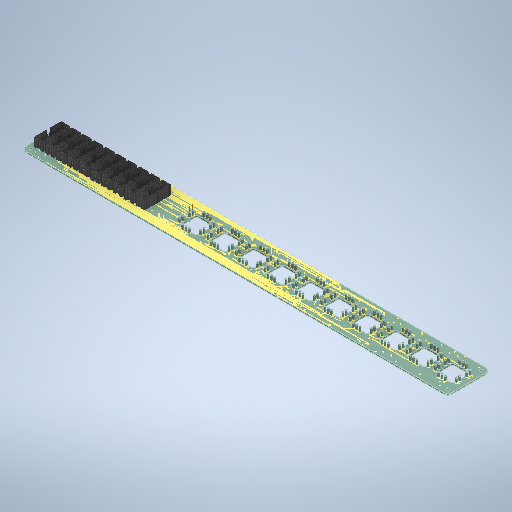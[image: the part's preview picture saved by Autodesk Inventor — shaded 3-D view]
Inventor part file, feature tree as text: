
AUTODESK INVENTOR PART (.ipt)
format: ipt  version: 2025.2 (Build 292293000, 293)  size: 19,431,936 bytes
history: native  units: mm
features: other x2, extrude x1, pattern_linear x1, sketch x1
ambient origin geometry x8: Origin, YZ Plane, XZ Plane, XY Plane, X Axis, Y Axis, Z Axis, Center Point
bodies: Volumenkörper1 (feature_tree), Volumenkörper2 (feature_tree), Volumenkörper3 (feature_tree), Volumenkörper4 (feature_tree), Volumenkörper5 (feature_tree), Volumenkörper6 (feature_tree), Volumenkörper7 (feature_tree), Volumenkörper8 (feature_tree), Volumenkörper9 (feature_tree), Volumenkörper10 (feature_tree), Volumenkörper11 (feature_tree), Volumenkörper12 (feature_tree), Volumenkörper13 (feature_tree), Volumenkörper14 (feature_tree), Volumenkörper15 (feature_tree), Volumenkörper16 (feature_tree), Volumenkörper17 (feature_tree), Volumenkörper18 (feature_tree), Volumenkörper19 (feature_tree), Volumenkörper20 (feature_tree), Volumenkörper21 (feature_tree), Volumenkörper22 (feature_tree), Volumenkörper23 (feature_tree), Volumenkörper24 (feature_tree), Volumenkörper25 (feature_tree), Volumenkörper26 (feature_tree), Volumenkörper27 (feature_tree), Volumenkörper28 (feature_tree), Volumenkörper29 (feature_tree), Volumenkörper30 (feature_tree), Volumenkörper31 (feature_tree), Volumenkörper32 (feature_tree), Volumenkörper33 (feature_tree), Volumenkörper34 (feature_tree), Volumenkörper35 (feature_tree), Volumenkörper36 (feature_tree), Volumenkörper37 (feature_tree), Volumenkörper38 (feature_tree), Volumenkörper39 (feature_tree), Volumenkörper40 (feature_tree), Volumenkörper41 (feature_tree), Volumenkörper42 (feature_tree), Volumenkörper43 (feature_tree), Volumenkörper44 (feature_tree), Volumenkörper45 (feature_tree), Volumenkörper46 (feature_tree), Volumenkörper47 (feature_tree), Volumenkörper48 (feature_tree), Volumenkörper49 (feature_tree), Volumenkörper50 (feature_tree), Volumenkörper51 (feature_tree), Volumenkörper52 (feature_tree), Volumenkörper53 (feature_tree), Volumenkörper54 (feature_tree), Volumenkörper55 (feature_tree), Volumenkörper56 (feature_tree), Volumenkörper57 (feature_tree), Volumenkörper58 (feature_tree), Volumenkörper59 (feature_tree), Volumenkörper60 (feature_tree), Volumenkörper61 (feature_tree), Volumenkörper62 (feature_tree), Volumenkörper63 (feature_tree), Volumenkörper64 (feature_tree), Volumenkörper65 (feature_tree), Volumenkörper66 (feature_tree), Volumenkörper67 (feature_tree), Volumenkörper68 (feature_tree), Volumenkörper69 (feature_tree), Volumenkörper70 (feature_tree), Volumenkörper71 (feature_tree), Volumenkörper72 (feature_tree), Volumenkörper73 (feature_tree), Volumenkörper74 (feature_tree), Volumenkörper75 (feature_tree), Volumenkörper76 (feature_tree), Volumenkörper77 (feature_tree), Volumenkörper78 (feature_tree), Volumenkörper79 (feature_tree), Volumenkörper80 (feature_tree), Volumenkörper81 (feature_tree), Volumenkörper82 (feature_tree), Volumenkörper83 (feature_tree), Volumenkörper84 (feature_tree), Volumenkörper85 (feature_tree), Volumenkörper86 (feature_tree), Volumenkörper87 (feature_tree), Volumenkörper88 (feature_tree), Volumenkörper89 (feature_tree), Volumenkörper90 (feature_tree), Volumenkörper91 (feature_tree), Volumenkörper92 (feature_tree), Volumenkörper93 (feature_tree), Volumenkörper94 (feature_tree), Volumenkörper95 (feature_tree), Volumenkörper96 (feature_tree), Volumenkörper97 (feature_tree), Volumenkörper98 (feature_tree), Volumenkörper99 (feature_tree), Volumenkörper100 (feature_tree), Volumenkörper101 (feature_tree), Volumenkörper102 (feature_tree), Volumenkörper103 (feature_tree), Volumenkörper104 (feature_tree), Volumenkörper105 (feature_tree), Volumenkörper106 (feature_tree), Volumenkörper107 (feature_tree), Volumenkörper108 (feature_tree), Volumenkörper109 (feature_tree), Volumenkörper110 (feature_tree), Volumenkörper111 (feature_tree), Volumenkörper112 (feature_tree), Volumenkörper113 (feature_tree), Volumenkörper114 (feature_tree), Volumenkörper115 (feature_tree), Volumenkörper116 (feature_tree), Volumenkörper117 (feature_tree), Volumenkörper118 (feature_tree), Volumenkörper119 (feature_tree), Volumenkörper120 (feature_tree), Volumenkörper121 (feature_tree), Volumenkörper122 (feature_tree), Volumenkörper123 (feature_tree), Volumenkörper124 (feature_tree), Volumenkörper125 (feature_tree), Volumenkörper126 (feature_tree), Volumenkörper127 (feature_tree), Volumenkörper128 (feature_tree), Volumenkörper129 (feature_tree), Volumenkörper130 (feature_tree), Volumenkörper131 (feature_tree), Volumenkörper132 (feature_tree), Volumenkörper133 (feature_tree), Volumenkörper134 (feature_tree), Volumenkörper135 (feature_tree), Volumenkörper136 (feature_tree), Volumenkörper137 (feature_tree), Volumenkörper138 (feature_tree), Volumenkörper139 (feature_tree), Volumenkörper140 (feature_tree), Volumenkörper141 (feature_tree), Volumenkörper142 (feature_tree), Volumenkörper143 (feature_tree), Volumenkörper144 (feature_tree), Volumenkörper145 (feature_tree), Volumenkörper146 (feature_tree), Volumenkörper147 (feature_tree), Volumenkörper148 (feature_tree), Volumenkörper149 (feature_tree), Volumenkörper150 (feature_tree), Volumenkörper151 (feature_tree), Volumenkörper152 (feature_tree), Volumenkörper153 (feature_tree), Volumenkörper154 (feature_tree), Volumenkörper155 (feature_tree), Volumenkörper156 (feature_tree), Volumenkörper157 (feature_tree), Volumenkörper158 (feature_tree), Volumenkörper159 (feature_tree), Volumenkörper160 (feature_tree), Volumenkörper161 (feature_tree), Volumenkörper162 (feature_tree), Volumenkörper163 (feature_tree), Volumenkörper164 (feature_tree), Volumenkörper165 (feature_tree), Volumenkörper166 (feature_tree), Volumenkörper167 (feature_tree), Volumenkörper168 (feature_tree), Volumenkörper169 (feature_tree), Volumenkörper170 (feature_tree), Volumenkörper171 (feature_tree), Volumenkörper172 (feature_tree), Volumenkörper173 (feature_tree), Volumenkörper174 (feature_tree), Volumenkörper175 (feature_tree), Volumenkörper176 (feature_tree), Volumenkörper177 (feature_tree), Volumenkörper178 (feature_tree), Volumenkörper179 (feature_tree), Volumenkörper180 (feature_tree), Volumenkörper181 (feature_tree), Volumenkörper182 (feature_tree), Volumenkörper183 (feature_tree), Volumenkörper184 (feature_tree), Volumenkörper185 (feature_tree), Volumenkörper186 (feature_tree), Volumenkörper187 (feature_tree), Volumenkörper188 (feature_tree), Volumenkörper189 (feature_tree), Volumenkörper190 (feature_tree), Volumenkörper191 (feature_tree), Volumenkörper192 (feature_tree), Volumenkörper193 (feature_tree), Volumenkörper194 (feature_tree), Volumenkörper195 (feature_tree), Volumenkörper196 (feature_tree), Volumenkörper197 (feature_tree), Volumenkörper198 (feature_tree), Volumenkörper199 (feature_tree), Volumenkörper200 (feature_tree), Volumenkörper201 (feature_tree), Volumenkörper202 (feature_tree), Volumenkörper203 (feature_tree), Volumenkörper204 (feature_tree), Volumenkörper205 (feature_tree), Volumenkörper206 (feature_tree), Volumenkörper207 (feature_tree), Volumenkörper208 (feature_tree), Volumenkörper209 (feature_tree), Volumenkörper210 (feature_tree), Volumenkörper211 (feature_tree), Volumenkörper212 (feature_tree), Volumenkörper213 (feature_tree), Volumenkörper214 (feature_tree), Volumenkörper215 (feature_tree), Volumenkörper216 (feature_tree), Volumenkörper217 (feature_tree), Volumenkörper218 (feature_tree), Volumenkörper219 (feature_tree), Volumenkörper220 (feature_tree), Volumenkörper221 (feature_tree), Volumenkörper222 (feature_tree), Volumenkörper223 (feature_tree), Volumenkörper224 (feature_tree), Volumenkörper225 (feature_tree), Volumenkörper226 (feature_tree), Volumenkörper227 (feature_tree), Volumenkörper228 (feature_tree), Volumenkörper229 (feature_tree), Volumenkörper230 (feature_tree), Volumenkörper231 (feature_tree), Volumenkörper232 (feature_tree), Volumenkörper233 (feature_tree), Volumenkörper234 (feature_tree), Volumenkörper235 (feature_tree), Volumenkörper236 (feature_tree), Volumenkörper237 (feature_tree), Volumenkörper238 (feature_tree), Volumenkörper239 (feature_tree), Volumenkörper240 (feature_tree), Volumenkörper241 (feature_tree), Volumenkörper242 (feature_tree), Volumenkörper243 (feature_tree), Volumenkörper244 (feature_tree), Volumenkörper245 (feature_tree), Volumenkörper246 (feature_tree), Volumenkörper247 (feature_tree), Volumenkörper248 (feature_tree), Volumenkörper249 (feature_tree), Volumenkörper250 (feature_tree), Volumenkörper251 (feature_tree), Volumenkörper252 (feature_tree), Volumenkörper253 (feature_tree), Volumenkörper254 (feature_tree), Volumenkörper255 (feature_tree), Volumenkörper256 (feature_tree), Volumenkörper257 (feature_tree), Volumenkörper258 (feature_tree), Volumenkörper259 (feature_tree), Volumenkörper260 (feature_tree), Volumenkörper261 (feature_tree), Volumenkörper262 (feature_tree), Volumenkörper263 (feature_tree), Volumenkörper264 (feature_tree), Volumenkörper265 (feature_tree), Volumenkörper266 (feature_tree), Volumenkörper267 (feature_tree), Volumenkörper268 (feature_tree), Volumenkörper269 (feature_tree), Volumenkörper270 (feature_tree), Volumenkörper271 (feature_tree), Volumenkörper272 (feature_tree), Volumenkörper273 (feature_tree), Volumenkörper274 (feature_tree), Volumenkörper275 (feature_tree), Volumenkörper276 (feature_tree), Volumenkörper277 (feature_tree), Volumenkörper278 (feature_tree), Volumenkörper279 (feature_tree), Volumenkörper280 (feature_tree), Volumenkörper281 (feature_tree), Volumenkörper282 (feature_tree), Volumenkörper283 (feature_tree), Volumenkörper284 (feature_tree), Volumenkörper285 (feature_tree), Volumenkörper286 (feature_tree), Volumenkörper287 (feature_tree), Volumenkörper288 (feature_tree), Volumenkörper289 (feature_tree), Volumenkörper290 (feature_tree), Volumenkörper291 (feature_tree), Volumenkörper292 (feature_tree), Volumenkörper293 (feature_tree), Volumenkörper294 (feature_tree), Volumenkörper295 (feature_tree), Volumenkörper296 (feature_tree), Volumenkörper297 (feature_tree), Volumenkörper298 (feature_tree), Volumenkörper299 (feature_tree), Volumenkörper300 (feature_tree), Volumenkörper301 (feature_tree), Volumenkörper302 (feature_tree), Volumenkörper303 (feature_tree), Volumenkörper304 (feature_tree), Volumenkörper305 (feature_tree), Volumenkörper306 (feature_tree), Volumenkörper307 (feature_tree), Volumenkörper308 (feature_tree), Volumenkörper309 (feature_tree), Volumenkörper310 (feature_tree), Volumenkörper311 (feature_tree), Volumenkörper312 (feature_tree), Volumenkörper313 (feature_tree), Volumenkörper314 (feature_tree), Volumenkörper315 (feature_tree), Volumenkörper316 (feature_tree), Volumenkörper317 (feature_tree), Volumenkörper318 (feature_tree), Volumenkörper319 (feature_tree), Volumenkörper320 (feature_tree), Volumenkörper321 (feature_tree), Volumenkörper322 (feature_tree), Volumenkörper323 (feature_tree), Volumenkörper324 (feature_tree), Volumenkörper325 (feature_tree), Volumenkörper326 (feature_tree), Volumenkörper327 (feature_tree), Volumenkörper328 (feature_tree), Volumenkörper329 (feature_tree), Volumenkörper330 (feature_tree), Volumenkörper331 (feature_tree), Volumenkörper332 (feature_tree), Volumenkörper333 (feature_tree), Volumenkörper334 (feature_tree), Volumenkörper335 (feature_tree), Volumenkörper336 (feature_tree), Volumenkörper337 (feature_tree), Volumenkörper338 (feature_tree), Volumenkörper339 (feature_tree), Volumenkörper340 (feature_tree), Volumenkörper341 (feature_tree), Volumenkörper342 (feature_tree), Volumenkörper343 (feature_tree), Volumenkörper344 (feature_tree), Volumenkörper345 (feature_tree), Volumenkörper346 (feature_tree), Volumenkörper347 (feature_tree), Volumenkörper348 (feature_tree), Volumenkörper349 (feature_tree), Volumenkörper350 (feature_tree), Volumenkörper351 (feature_tree), Volumenkörper352 (feature_tree), Volumenkörper353 (feature_tree), Volumenkörper354 (feature_tree), Volumenkörper355 (feature_tree), Volumenkörper356 (feature_tree), Volumenkörper357 (feature_tree), Volumenkörper358 (feature_tree), Volumenkörper359 (feature_tree), Volumenkörper360 (feature_tree), Volumenkörper361 (feature_tree), Volumenkörper362 (feature_tree), Volumenkörper363 (feature_tree), Volumenkörper364 (feature_tree), Volumenkörper365 (feature_tree), Volumenkörper366 (feature_tree), Volumenkörper367 (feature_tree), Volumenkörper368 (feature_tree), Volumenkörper369 (feature_tree), Volumenkörper370 (feature_tree), Volumenkörper371 (feature_tree), Volumenkörper372 (feature_tree), Volumenkörper373 (feature_tree), Volumenkörper374 (feature_tree), Volumenkörper375 (feature_tree), Volumenkörper376 (feature_tree), Volumenkörper377 (feature_tree), Volumenkörper378 (feature_tree), Volumenkörper379 (feature_tree), Volumenkörper380 (feature_tree), Volumenkörper381 (feature_tree), Volumenkörper382 (feature_tree), Volumenkörper383 (feature_tree), Volumenkörper384 (feature_tree), Volumenkörper385 (feature_tree), Volumenkörper386 (feature_tree), Volumenkörper387 (feature_tree), Volumenkörper388 (feature_tree), Volumenkörper389 (feature_tree), Volumenkörper390 (feature_tree), Volumenkörper391 (feature_tree), Volumenkörper392 (feature_tree), Volumenkörper393 (feature_tree), Volumenkörper394 (feature_tree), Volumenkörper395 (feature_tree), Volumenkörper396 (feature_tree), Volumenkörper397 (feature_tree), Volumenkörper398 (feature_tree), Volumenkörper399 (feature_tree), Volumenkörper400 (feature_tree), Volumenkörper401 (feature_tree), Volumenkörper402 (feature_tree), Volumenkörper403 (feature_tree), Volumenkörper404 (feature_tree), Volumenkörper405 (feature_tree), Volumenkörper406 (feature_tree), Volumenkörper407 (feature_tree), Volumenkörper408 (feature_tree), Volumenkörper409 (feature_tree), Volumenkörper410 (feature_tree), Volumenkörper411 (feature_tree), Volumenkörper412 (feature_tree), Volumenkörper413 (feature_tree), Volumenkörper414 (feature_tree), Volumenkörper415 (feature_tree), Volumenkörper416 (feature_tree), Volumenkörper417 (feature_tree), Volumenkörper418 (feature_tree), Volumenkörper419 (feature_tree), Volumenkörper420 (feature_tree), Volumenkörper421 (feature_tree), Volumenkörper422 (feature_tree), Volumenkörper423 (feature_tree), Volumenkörper424 (feature_tree), Volumenkörper425 (feature_tree), Volumenkörper426 (feature_tree), Volumenkörper427 (feature_tree), Volumenkörper428 (feature_tree), Volumenkörper429 (feature_tree), Volumenkörper430 (feature_tree), Volumenkörper431 (feature_tree), Volumenkörper432 (feature_tree), Volumenkörper433 (feature_tree), Volumenkörper434 (feature_tree), Volumenkörper435 (feature_tree), Volumenkörper436 (feature_tree), Volumenkörper437 (feature_tree), Volumenkörper438 (feature_tree), Volumenkörper439 (feature_tree), Volumenkörper440 (feature_tree), Volumenkörper441 (feature_tree), Volumenkörper442 (feature_tree), Volumenkörper443 (feature_tree), Volumenkörper444 (feature_tree), Volumenkörper445 (feature_tree), Volumenkörper446 (feature_tree), Volumenkörper447 (feature_tree), Volumenkörper448 (feature_tree), Volumenkörper449 (feature_tree), Volumenkörper450 (feature_tree), Volumenkörper451 (feature_tree), Volumenkörper452 (feature_tree), Volumenkörper453 (feature_tree), Volumenkörper454 (feature_tree), Volumenkörper455 (feature_tree), Volumenkörper456 (feature_tree), Volumenkörper457 (feature_tree), Volumenkörper458 (feature_tree), Volumenkörper459 (feature_tree), Volumenkörper460 (feature_tree), Volumenkörper461 (feature_tree), Volumenkörper462 (feature_tree), Volumenkörper463 (feature_tree), Volumenkörper464 (feature_tree), Volumenkörper465 (feature_tree), Volumenkörper466 (feature_tree), Volumenkörper467 (feature_tree), Volumenkörper468 (feature_tree), Volumenkörper469 (feature_tree), Volumenkörper470 (feature_tree), Volumenkörper471 (feature_tree), Volumenkörper472 (feature_tree), Volumenkörper473 (feature_tree), Volumenkörper474 (feature_tree), Volumenkörper475 (feature_tree), Volumenkörper476 (feature_tree), Volumenkörper477 (feature_tree), Volumenkörper478 (feature_tree), Volumenkörper479 (feature_tree), Volumenkörper480 (feature_tree), Volumenkörper481 (feature_tree), Volumenkörper482 (feature_tree), Volumenkörper483 (feature_tree), Volumenkörper484 (feature_tree), Volumenkörper485 (feature_tree), Volumenkörper486 (feature_tree), Volumenkörper487 (feature_tree), Volumenkörper488 (feature_tree), Volumenkörper489 (feature_tree), Volumenkörper490 (feature_tree), Volumenkörper491 (feature_tree), Volumenkörper492 (feature_tree), Volumenkörper493 (feature_tree), Volumenkörper494 (feature_tree), Volumenkörper495 (feature_tree), Volumenkörper496 (feature_tree), Volumenkörper497 (feature_tree), Volumenkörper498 (feature_tree), Volumenkörper499 (feature_tree), Volumenkörper500 (feature_tree), Volumenkörper501 (feature_tree), Volumenkörper502 (feature_tree), Volumenkörper503 (feature_tree), Volumenkörper504 (feature_tree), Volumenkörper505 (feature_tree), Volumenkörper506 (feature_tree), Volumenkörper507 (feature_tree), Volumenkörper508 (feature_tree), Volumenkörper509 (feature_tree), Volumenkörper510 (feature_tree), Volumenkörper511 (feature_tree), Volumenkörper512 (feature_tree), Volumenkörper513 (feature_tree), Volumenkörper514 (feature_tree), Volumenkörper515 (feature_tree), Volumenkörper516 (feature_tree), Volumenkörper517 (feature_tree), Volumenkörper518 (feature_tree), Volumenkörper519 (feature_tree), Volumenkörper520 (feature_tree), Volumenkörper521 (feature_tree), Volumenkörper522 (feature_tree), Volumenkörper523 (feature_tree), Volumenkörper524 (feature_tree), Volumenkörper525 (feature_tree), Volumenkörper526 (feature_tree), Volumenkörper527 (feature_tree), Volumenkörper528 (feature_tree), Volumenkörper529 (feature_tree), Volumenkörper530 (feature_tree), Volumenkörper531 (feature_tree), Volumenkörper532 (feature_tree), Volumenkörper533 (feature_tree), Volumenkörper534 (feature_tree), Volumenkörper535 (feature_tree), Volumenkörper536 (feature_tree), Volumenkörper537 (feature_tree), Volumenkörper538 (feature_tree), Volumenkörper539 (feature_tree), Volumenkörper540 (feature_tree), Volumenkörper541 (feature_tree), Volumenkörper542 (feature_tree), Volumenkörper543 (feature_tree), Volumenkörper544 (feature_tree), Volumenkörper545 (feature_tree), Volumenkörper546 (feature_tree), Volumenkörper547 (feature_tree), Volumenkörper548 (feature_tree), Volumenkörper549 (feature_tree), Volumenkörper550 (feature_tree), Volumenkörper551 (feature_tree), Volumenkörper552 (feature_tree), Volumenkörper553 (feature_tree), Volumenkörper554 (feature_tree), Volumenkörper555 (feature_tree), Volumenkörper556 (feature_tree), Volumenkörper557 (feature_tree), Volumenkörper558 (feature_tree), Volumenkörper559 (feature_tree), Volumenkörper560 (feature_tree), Volumenkörper561 (feature_tree), Volumenkörper562 (feature_tree), Volumenkörper563 (feature_tree), Volumenkörper564 (feature_tree), Volumenkörper565 (feature_tree), Volumenkörper566 (feature_tree), Volumenkörper567 (feature_tree), Volumenkörper568 (feature_tree), Volumenkörper569 (feature_tree), Volumenkörper570 (feature_tree), Volumenkörper571 (feature_tree), Volumenkörper572 (feature_tree), Volumenkörper573 (feature_tree), Volumenkörper574 (feature_tree), Volumenkörper575 (feature_tree), Volumenkörper576 (feature_tree), Volumenkörper577 (feature_tree), Volumenkörper578 (feature_tree), Volumenkörper579 (feature_tree), Volumenkörper580 (feature_tree), Volumenkörper581 (feature_tree), Volumenkörper582 (feature_tree), Volumenkörper583 (feature_tree), Volumenkörper584 (feature_tree), Volumenkörper585 (feature_tree), Volumenkörper586 (feature_tree), Volumenkörper587 (feature_tree), Volumenkörper588 (feature_tree), Volumenkörper589 (feature_tree), Volumenkörper590 (feature_tree), Volumenkörper591 (feature_tree), Volumenkörper592 (feature_tree), Volumenkörper593 (feature_tree), Volumenkörper594 (feature_tree), Volumenkörper595 (feature_tree), Volumenkörper596 (feature_tree), Volumenkörper597 (feature_tree), Volumenkörper598 (feature_tree), Volumenkörper599 (feature_tree), Volumenkörper600 (feature_tree), Volumenkörper601 (feature_tree), Volumenkörper602 (feature_tree), Volumenkörper603 (feature_tree), Volumenkörper604 (feature_tree), Volumenkörper605 (feature_tree), Volumenkörper606 (feature_tree), Volumenkörper607 (feature_tree), Volumenkörper608 (feature_tree), Volumenkörper609 (feature_tree), Volumenkörper610 (feature_tree), Volumenkörper611 (feature_tree), Volumenkörper612 (feature_tree), Volumenkörper613 (feature_tree), Volumenkörper614 (feature_tree), Volumenkörper615 (feature_tree), Volumenkörper616 (feature_tree), Volumenkörper617 (feature_tree), Volumenkörper618 (feature_tree), Volumenkörper619 (feature_tree), Volumenkörper620 (feature_tree), Volumenkörper621 (feature_tree), Volumenkörper622 (feature_tree), Volumenkörper623 (feature_tree), Volumenkörper624 (feature_tree), Volumenkörper625 (feature_tree), Volumenkörper626 (feature_tree), Volumenkörper627 (feature_tree), Volumenkörper628 (feature_tree), Volumenkörper629 (feature_tree), Volumenkörper630 (feature_tree), Volumenkörper631 (feature_tree), Volumenkörper632 (feature_tree), Volumenkörper633 (feature_tree), Volumenkörper634 (feature_tree), Volumenkörper635 (feature_tree), Volumenkörper636 (feature_tree), Volumenkörper637 (feature_tree), Volumenkörper638 (feature_tree), Volumenkörper639 (feature_tree), Volumenkörper640 (feature_tree), Volumenkörper641 (feature_tree), Volumenkörper642 (feature_tree), Volumenkörper643 (feature_tree), Volumenkörper644 (feature_tree), Volumenkörper645 (feature_tree), Volumenkörper646 (feature_tree), Volumenkörper647 (feature_tree), Volumenkörper648 (feature_tree), Volumenkörper649 (feature_tree), Volumenkörper650 (feature_tree), Volumenkörper651 (feature_tree), Volumenkörper652 (feature_tree), Volumenkörper653 (feature_tree), Volumenkörper654 (feature_tree), Volumenkörper655 (feature_tree), Volumenkörper656 (feature_tree), Volumenkörper657 (feature_tree), Volumenkörper658 (feature_tree), Volumenkörper659 (feature_tree), Volumenkörper660 (feature_tree), Volumenkörper661 (feature_tree), Volumenkörper662 (feature_tree), Volumenkörper663 (feature_tree), Volumenkörper664 (feature_tree), Volumenkörper665 (feature_tree), Volumenkörper666 (feature_tree), Volumenkörper667 (feature_tree), Volumenkörper668 (feature_tree), Volumenkörper669 (feature_tree), Volumenkörper670 (feature_tree), Volumenkörper671 (feature_tree), Volumenkörper672 (feature_tree), Volumenkörper673 (feature_tree), Volumenkörper674 (feature_tree), Volumenkörper675 (feature_tree), Volumenkörper676 (feature_tree), Volumenkörper677 (feature_tree), Volumenkörper678 (feature_tree), Volumenkörper679 (feature_tree), Volumenkörper680 (feature_tree), Volumenkörper681 (feature_tree), Volumenkörper682 (feature_tree), Volumenkörper683 (feature_tree), Volumenkörper684 (feature_tree), Volumenkörper685 (feature_tree), Volumenkörper686 (feature_tree), Volumenkörper687 (feature_tree), Volumenkörper688 (feature_tree), Volumenkörper689 (feature_tree), Volumenkörper690 (feature_tree), Volumenkörper691 (feature_tree), Volumenkörper692 (feature_tree), Volumenkörper693 (feature_tree), Volumenkörper694 (feature_tree), Volumenkörper695 (feature_tree), Volumenkörper696 (feature_tree), Volumenkörper697 (feature_tree), Volumenkörper698 (feature_tree), Volumenkörper699 (feature_tree), Volumenkörper700 (feature_tree), Volumenkörper701 (feature_tree), Volumenkörper702 (feature_tree), Volumenkörper703 (feature_tree), Volumenkörper704 (feature_tree), Volumenkörper705 (feature_tree), Volumenkörper706 (feature_tree), Volumenkörper707 (feature_tree), Volumenkörper708 (feature_tree), Volumenkörper709 (feature_tree), Volumenkörper710 (feature_tree), Volumenkörper711 (feature_tree), Volumenkörper712 (feature_tree), Volumenkörper713 (feature_tree), Volumenkörper714 (feature_tree), Volumenkörper715 (feature_tree), Volumenkörper716 (feature_tree), Volumenkörper717 (feature_tree), Volumenkörper718 (feature_tree), Volumenkörper719 (feature_tree), Volumenkörper720 (feature_tree), Volumenkörper721 (feature_tree), Volumenkörper722 (feature_tree), Volumenkörper723 (feature_tree), Volumenkörper724 (feature_tree), Volumenkörper725 (feature_tree), Volumenkörper726 (feature_tree), Volumenkörper727 (feature_tree), Volumenkörper728 (feature_tree), Volumenkörper729 (feature_tree), Volumenkörper730 (feature_tree), Volumenkörper731 (feature_tree), Volumenkörper732 (feature_tree), Volumenkörper733 (feature_tree), Volumenkörper734 (feature_tree), Volumenkörper735 (feature_tree), Volumenkörper736 (feature_tree), Volumenkörper737 (feature_tree), Volumenkörper738 (feature_tree), Volumenkörper739 (feature_tree), Volumenkörper740 (feature_tree), Volumenkörper741 (feature_tree), Volumenkörper742 (feature_tree), Volumenkörper743 (feature_tree), Volumenkörper744 (feature_tree), Volumenkörper745 (feature_tree), Volumenkörper746 (feature_tree), Volumenkörper747 (feature_tree), Volumenkörper748 (feature_tree), Volumenkörper749 (feature_tree), Volumenkörper750 (feature_tree), Volumenkörper751 (feature_tree), Volumenkörper752 (feature_tree), Volumenkörper753 (feature_tree), Volumenkörper754 (feature_tree), Volumenkörper755 (feature_tree), Volumenkörper756 (feature_tree), Volumenkörper757 (feature_tree), Volumenkörper758 (feature_tree), Volumenkörper759 (feature_tree), Volumenkörper760 (feature_tree), Volumenkörper761 (feature_tree), Volumenkörper762 (feature_tree), Volumenkörper763 (feature_tree), Volumenkörper764 (feature_tree), Volumenkörper765 (feature_tree), Volumenkörper766 (feature_tree), Volumenkörper767 (feature_tree), Volumenkörper768 (feature_tree), Volumenkörper769 (feature_tree), Volumenkörper770 (feature_tree), Volumenkörper771 (feature_tree), Volumenkörper772 (feature_tree), Volumenkörper773 (feature_tree), Volumenkörper774 (feature_tree), Volumenkörper775 (feature_tree), Volumenkörper776 (feature_tree), Volumenkörper777 (feature_tree), Volumenkörper778 (feature_tree), Volumenkörper779 (feature_tree), Volumenkörper780 (feature_tree), Volumenkörper781 (feature_tree), Volumenkörper782 (feature_tree), Volumenkörper783 (feature_tree), Volumenkörper784 (feature_tree), Volumenkörper785 (feature_tree), Volumenkörper786 (feature_tree), Volumenkörper787 (feature_tree), Volumenkörper788 (feature_tree), Volumenkörper789 (feature_tree), Volumenkörper790 (feature_tree), Volumenkörper791 (feature_tree), Volumenkörper792 (feature_tree), Volumenkörper793 (feature_tree), Volumenkörper794 (feature_tree), Volumenkörper795 (feature_tree), Volumenkörper796 (feature_tree), Volumenkörper797 (feature_tree), Volumenkörper798 (feature_tree), Volumenkörper799 (feature_tree), Volumenkörper800 (feature_tree), Volumenkörper801 (feature_tree), Volumenkörper802 (feature_tree), Volumenkörper803 (feature_tree), Volumenkörper804 (feature_tree), Volumenkörper805 (feature_tree), Volumenkörper806 (feature_tree), Volumenkörper807 (feature_tree), Volumenkörper808 (feature_tree), Volumenkörper809 (feature_tree), Volumenkörper810 (feature_tree), Volumenkörper811 (feature_tree), Volumenkörper812 (feature_tree), Volumenkörper813 (feature_tree), Volumenkörper814 (feature_tree), Volumenkörper815 (feature_tree), Volumenkörper816 (feature_tree), Volumenkörper817 (feature_tree), Volumenkörper818 (feature_tree), Volumenkörper819 (feature_tree), Volumenkörper820 (feature_tree), Volumenkörper821 (feature_tree), Volumenkörper822 (feature_tree), Volumenkörper823 (feature_tree), Volumenkörper824 (feature_tree), Volumenkörper825 (feature_tree), Volumenkörper826 (feature_tree), Volumenkörper827 (feature_tree), Volumenkörper828 (feature_tree), Volumenkörper829 (feature_tree), Volumenkörper830 (feature_tree), Volumenkörper831 (feature_tree), Volumenkörper832 (feature_tree), Volumenkörper833 (feature_tree), Volumenkörper834 (feature_tree), Volumenkörper835 (feature_tree), Volumenkörper836 (feature_tree), Volumenkörper837 (feature_tree), Volumenkörper838 (feature_tree), Volumenkörper839 (feature_tree), Volumenkörper840 (feature_tree), Volumenkörper841 (feature_tree), Volumenkörper842 (feature_tree), Volumenkörper843 (feature_tree), Volumenkörper844 (feature_tree), Volumenkörper845 (feature_tree), Volumenkörper846 (feature_tree), Volumenkörper847 (feature_tree), Volumenkörper848 (feature_tree), Volumenkörper849 (feature_tree), Volumenkörper850 (feature_tree), Volumenkörper851 (feature_tree), Volumenkörper852 (feature_tree), Volumenkörper853 (feature_tree), Volumenkörper854 (feature_tree), Volumenkörper855 (feature_tree), Volumenkörper856 (feature_tree), Volumenkörper857 (feature_tree), Volumenkörper858 (feature_tree), Volumenkörper859 (feature_tree), Volumenkörper860 (feature_tree), Volumenkörper861 (feature_tree), Volumenkörper862 (feature_tree), Volumenkörper863 (feature_tree), Volumenkörper864 (feature_tree), Volumenkörper865 (feature_tree), Volumenkörper866 (feature_tree), Volumenkörper867 (feature_tree), Volumenkörper868 (feature_tree), Volumenkörper869 (feature_tree), Volumenkörper870 (feature_tree), Volumenkörper871 (feature_tree), Volumenkörper872 (feature_tree), Volumenkörper873 (feature_tree), Volumenkörper874 (feature_tree), Volumenkörper875 (feature_tree), Volumenkörper876 (feature_tree), Volumenkörper877 (feature_tree), Volumenkörper878 (feature_tree), Volumenkörper879 (feature_tree), Volumenkörper880 (feature_tree), Volumenkörper881 (feature_tree), Volumenkörper882 (feature_tree), Volumenkörper883 (feature_tree), Volumenkörper884 (feature_tree), Volumenkörper885 (feature_tree), Volumenkörper886 (feature_tree), Volumenkörper887 (feature_tree), Volumenkörper888 (feature_tree), Volumenkörper889 (feature_tree), Volumenkörper890 (feature_tree), Volumenkörper891 (feature_tree), Volumenkörper892 (feature_tree), Volumenkörper893 (feature_tree), Volumenkörper894 (feature_tree), Volumenkörper895 (feature_tree), Volumenkörper896 (feature_tree), Volumenkörper897 (feature_tree), Volumenkörper898 (feature_tree), Volumenkörper899 (feature_tree), Volumenkörper900 (feature_tree), Volumenkörper901 (feature_tree), Volumenkörper902 (feature_tree), Volumenkörper903 (feature_tree), Volumenkörper904 (feature_tree), Volumenkörper905 (feature_tree), Volumenkörper906 (feature_tree), Volumenkörper907 (feature_tree), Volumenkörper908 (feature_tree), Volumenkörper909 (feature_tree), Volumenkörper910 (feature_tree), Volumenkörper911 (feature_tree), Volumenkörper912 (feature_tree), Volumenkörper913 (feature_tree), Volumenkörper914 (feature_tree), Volumenkörper915 (feature_tree), Volumenkörper916 (feature_tree), Volumenkörper917 (feature_tree), Volumenkörper918 (feature_tree), Volumenkörper919 (feature_tree), Volumenkörper920 (feature_tree), Volumenkörper921 (feature_tree), Volumenkörper922 (feature_tree), Volumenkörper923 (feature_tree), Volumenkörper924 (feature_tree), Volumenkörper925 (feature_tree), Volumenkörper926 (feature_tree), Volumenkörper927 (feature_tree), Volumenkörper928 (feature_tree), Volumenkörper929 (feature_tree), Volumenkörper930 (feature_tree), Volumenkörper931 (feature_tree), Volumenkörper932 (feature_tree), Volumenkörper933 (feature_tree), Volumenkörper934 (feature_tree), Volumenkörper935 (feature_tree), Volumenkörper936 (feature_tree), Volumenkörper937 (feature_tree), Volumenkörper938 (feature_tree), Volumenkörper939 (feature_tree), Volumenkörper940 (feature_tree), Volumenkörper941 (feature_tree), Volumenkörper942 (feature_tree), Volumenkörper943 (feature_tree), Volumenkörper944 (feature_tree), Volumenkörper945 (feature_tree), Volumenkörper946 (feature_tree), Volumenkörper947 (feature_tree), Volumenkörper948 (feature_tree), Volumenkörper949 (feature_tree), Volumenkörper950 (feature_tree), Volumenkörper951 (feature_tree), Volumenkörper952 (feature_tree), Volumenkörper953 (feature_tree), Volumenkörper954 (feature_tree), Volumenkörper955 (feature_tree), Volumenkörper956 (feature_tree), Volumenkörper957 (feature_tree), Volumenkörper958 (feature_tree), Volumenkörper959 (feature_tree), Volumenkörper960 (feature_tree), Volumenkörper961 (feature_tree), Volumenkörper962 (feature_tree), Volumenkörper963 (feature_tree), Volumenkörper964 (feature_tree), Volumenkörper965 (feature_tree), Volumenkörper966 (feature_tree), Volumenkörper967 (feature_tree), Volumenkörper968 (feature_tree), Volumenkörper969 (feature_tree), Volumenkörper970 (feature_tree), Volumenkörper971 (feature_tree), Volumenkörper972 (feature_tree), Volumenkörper973 (feature_tree), Volumenkörper974 (feature_tree), Volumenkörper975 (feature_tree), Volumenkörper976 (feature_tree), Volumenkörper977 (feature_tree), Volumenkörper978 (feature_tree), Volumenkörper979 (feature_tree), Volumenkörper980 (feature_tree), Volumenkörper981 (feature_tree), Volumenkörper982 (feature_tree), Volumenkörper983 (feature_tree), Volumenkörper984 (feature_tree), Volumenkörper985 (feature_tree), Volumenkörper986 (feature_tree), Volumenkörper987 (feature_tree), Volumenkörper988 (feature_tree), Volumenkörper989 (feature_tree), Volumenkörper990 (feature_tree), Volumenkörper991 (feature_tree), Volumenkörper992 (feature_tree), Volumenkörper993 (feature_tree), Volumenkörper994 (feature_tree), Volumenkörper995 (feature_tree), Volumenkörper996 (feature_tree), Volumenkörper997 (feature_tree), Volumenkörper998 (feature_tree), Volumenkörper999 (feature_tree), Volumenkörper1000 (feature_tree), Volumenkörper1001 (feature_tree), Volumenkörper1002 (feature_tree), Volumenkörper1003 (feature_tree), Volumenkörper1004 (feature_tree), Volumenkörper1005 (feature_tree), Volumenkörper1006 (feature_tree), Volumenkörper1007 (feature_tree), Volumenkörper1008 (feature_tree), Volumenkörper1009 (feature_tree), Volumenkörper1010 (feature_tree), Volumenkörper1011 (feature_tree), Volumenkörper1012 (feature_tree), Volumenkörper1013 (feature_tree), Volumenkörper1014 (feature_tree), Volumenkörper1015 (feature_tree), Volumenkörper1016 (feature_tree), Volumenkörper1017 (feature_tree), Volumenkörper1018 (feature_tree), Volumenkörper1019 (feature_tree), Volumenkörper1020 (feature_tree), Volumenkörper1021 (feature_tree), Volumenkörper1022 (feature_tree), Volumenkörper1023 (feature_tree), Volumenkörper1024 (feature_tree), Volumenkörper1025 (feature_tree), Volumenkörper1026 (feature_tree), Volumenkörper1027 (feature_tree), Volumenkörper1028 (feature_tree), Volumenkörper1029 (feature_tree), Volumenkörper1030 (feature_tree), Volumenkörper1031 (feature_tree), Volumenkörper1032 (feature_tree), Volumenkörper1033 (feature_tree), Volumenkörper1034 (feature_tree), Volumenkörper1035 (feature_tree), Volumenkörper1036 (feature_tree), Volumenkörper1037 (feature_tree), Volumenkörper1038 (feature_tree), Volumenkörper1039 (feature_tree), Volumenkörper1040 (feature_tree), Volumenkörper1041 (feature_tree), Volumenkörper1042 (feature_tree), Volumenkörper1043 (feature_tree), Volumenkörper1044 (feature_tree), Volumenkörper1045 (feature_tree), Volumenkörper1046 (feature_tree), Volumenkörper1047 (feature_tree), Volumenkörper1048 (feature_tree), Volumenkörper1049 (feature_tree), Volumenkörper1050 (feature_tree), Volumenkörper1051 (feature_tree), Volumenkörper1052 (feature_tree), Volumenkörper1053 (feature_tree), Volumenkörper1054 (feature_tree), Volumenkörper1055 (feature_tree), Volumenkörper1056 (feature_tree), Volumenkörper1057 (feature_tree), Volumenkörper1058 (feature_tree), Volumenkörper1059 (feature_tree), Volumenkörper1060 (feature_tree), Volumenkörper1061 (feature_tree), Volumenkörper1062 (feature_tree), Volumenkörper1063 (feature_tree), Volumenkörper1064 (feature_tree), Volumenkörper1065 (feature_tree), Volumenkörper1066 (feature_tree), Volumenkörper1067 (feature_tree), Volumenkörper1068 (feature_tree), Volumenkörper1069 (feature_tree), Volumenkörper1070 (feature_tree), Volumenkörper1071 (feature_tree), Volumenkörper1072 (feature_tree), Volumenkörper1073 (feature_tree), Volumenkörper1074 (feature_tree), Volumenkörper1075 (feature_tree), Volumenkörper1076 (feature_tree), Volumenkörper1077 (feature_tree), Volumenkörper1078 (feature_tree), Volumenkörper1079 (feature_tree), Volumenkörper1080 (feature_tree), Volumenkörper1081 (feature_tree), Volumenkörper1082 (feature_tree), Volumenkörper1083 (feature_tree), Volumenkörper1084 (feature_tree), Volumenkörper1085 (feature_tree), Volumenkörper1086 (feature_tree), Volumenkörper1087 (feature_tree), Volumenkörper1088 (feature_tree), Volumenkörper1089 (feature_tree), Volumenkörper1090 (feature_tree), Volumenkörper1091 (feature_tree), Volumenkörper1092 (feature_tree), Volumenkörper1093 (feature_tree), Volumenkörper1094 (feature_tree), Volumenkörper1095 (feature_tree), Volumenkörper1096 (feature_tree), Volumenkörper1097 (feature_tree), Volumenkörper1098 (feature_tree), Volumenkörper1099 (feature_tree), Volumenkörper1100 (feature_tree), Volumenkörper1101 (feature_tree), Volumenkörper1102 (feature_tree), Volumenkörper1103 (feature_tree), Volumenkörper1104 (feature_tree), Volumenkörper1105 (feature_tree), Volumenkörper1106 (feature_tree), Volumenkörper1107 (feature_tree), Volumenkörper1108 (feature_tree), Volumenkörper1109 (feature_tree), Volumenkörper1110 (feature_tree), Volumenkörper1111 (feature_tree), Volumenkörper1112 (feature_tree), Volumenkörper1113 (feature_tree), Volumenkörper1114 (feature_tree), Volumenkörper1115 (feature_tree), Volumenkörper1116 (feature_tree), Volumenkörper1117 (feature_tree), Volumenkörper1118 (feature_tree), Volumenkörper1119 (feature_tree), Volumenkörper1120 (feature_tree), Volumenkörper1121 (feature_tree), Volumenkörper1122 (feature_tree), Volumenkörper1123 (feature_tree), Volumenkörper1124 (feature_tree), Volumenkörper1125 (feature_tree), Volumenkörper1126 (feature_tree), Volumenkörper1127 (feature_tree), Volumenkörper1128 (feature_tree), Volumenkörper1129 (feature_tree), Volumenkörper1130 (feature_tree), Volumenkörper1131 (feature_tree), Volumenkörper1132 (feature_tree), Volumenkörper1133 (feature_tree), Volumenkörper1134 (feature_tree), Volumenkörper1135 (feature_tree), Volumenkörper1136 (feature_tree), Volumenkörper1137 (feature_tree), Volumenkörper1138 (feature_tree), Volumenkörper1139 (feature_tree), Volumenkörper1140 (feature_tree), Volumenkörper1141 (feature_tree), Volumenkörper1142 (feature_tree), Volumenkörper1143 (feature_tree), Volumenkörper1144 (feature_tree), Volumenkörper1145 (feature_tree), Volumenkörper1146 (feature_tree), Volumenkörper1147 (feature_tree), Volumenkörper1148 (feature_tree), Volumenkörper1149 (feature_tree), Volumenkörper1150 (feature_tree), Volumenkörper1151 (feature_tree), Volumenkörper1152 (feature_tree), Volumenkörper1153 (feature_tree), Volumenkörper1154 (feature_tree), Volumenkörper1155 (feature_tree), Volumenkörper1156 (feature_tree), Volumenkörper1157 (feature_tree), Volumenkörper1158 (feature_tree), Volumenkörper1159 (feature_tree), Volumenkörper1160 (feature_tree), Volumenkörper1161 (feature_tree), Volumenkörper1162 (feature_tree), Volumenkörper1163 (feature_tree), Volumenkörper1164 (feature_tree), Volumenkörper1165 (feature_tree), Volumenkörper1166 (feature_tree), Volumenkörper1167 (feature_tree), Volumenkörper1168 (feature_tree), Volumenkörper1169 (feature_tree), Volumenkörper1170 (feature_tree), Volumenkörper1171 (feature_tree), Volumenkörper1172 (feature_tree), Volumenkörper1173 (feature_tree), Volumenkörper1174 (feature_tree), Volumenkörper1175 (feature_tree), Volumenkörper1176 (feature_tree), Volumenkörper1177 (feature_tree), Volumenkörper1178 (feature_tree), Volumenkörper1179 (feature_tree), Volumenkörper1180 (feature_tree), Volumenkörper1181 (feature_tree), Volumenkörper1182 (feature_tree), Volumenkörper1183 (feature_tree), Volumenkörper1184 (feature_tree), Volumenkörper1185 (feature_tree), Volumenkörper1186 (feature_tree), Volumenkörper1187 (feature_tree), Volumenkörper1188 (feature_tree), Volumenkörper1189 (feature_tree), Volumenkörper1190 (feature_tree), Volumenkörper1191 (feature_tree), Volumenkörper1192 (feature_tree), Volumenkörper1193 (feature_tree), Volumenkörper1194 (feature_tree), Volumenkörper1195 (feature_tree), Volumenkörper1196 (feature_tree), Volumenkörper1197 (feature_tree), Volumenkörper1198 (feature_tree), Volumenkörper1199 (feature_tree), Volumenkörper1200 (feature_tree), Volumenkörper1201 (feature_tree), Volumenkörper1202 (feature_tree), Volumenkörper1203 (feature_tree), Volumenkörper1204 (feature_tree), Volumenkörper1205 (feature_tree), Volumenkörper1206 (feature_tree), Volumenkörper1207 (feature_tree), Volumenkörper1208 (feature_tree), Volumenkörper1209 (feature_tree), Volumenkörper1210 (feature_tree), Volumenkörper1211 (feature_tree), Volumenkörper1212 (feature_tree), Volumenkörper1213 (feature_tree), Volumenkörper1214 (feature_tree), Volumenkörper1215 (feature_tree), Volumenkörper1216 (feature_tree), Volumenkörper1217 (feature_tree), Volumenkörper1218 (feature_tree), Volumenkörper1219 (feature_tree), Volumenkörper1220 (feature_tree), Volumenkörper1221 (feature_tree), Volumenkörper1222 (feature_tree), Volumenkörper1223 (feature_tree), Volumenkörper1224 (feature_tree), Volumenkörper1225 (feature_tree), Volumenkörper1226 (feature_tree), Volumenkörper1227 (feature_tree), Volumenkörper1228 (feature_tree), Volumenkörper1229 (feature_tree), Volumenkörper1230 (feature_tree), Volumenkörper1231 (feature_tree), Volumenkörper1232 (feature_tree), Volumenkörper1233 (feature_tree), Volumenkörper1234 (feature_tree), Volumenkörper1235 (feature_tree), Volumenkörper1236 (feature_tree), Volumenkörper1237 (feature_tree), Volumenkörper1238 (feature_tree), Volumenkörper1239 (feature_tree), Volumenkörper1240 (feature_tree), Volumenkörper1241 (feature_tree), Volumenkörper1242 (feature_tree), Volumenkörper1243 (feature_tree), Volumenkörper1244 (feature_tree), Volumenkörper1245 (feature_tree), Volumenkörper1246 (feature_tree), Volumenkörper1247 (feature_tree), Volumenkörper1248 (feature_tree), Volumenkörper1249 (feature_tree), Volumenkörper1250 (feature_tree), Volumenkörper1251 (feature_tree), Volumenkörper1252 (feature_tree), Volumenkörper1253 (feature_tree), Volumenkörper1254 (feature_tree), Volumenkörper1255 (feature_tree), Volumenkörper1256 (feature_tree), Volumenkörper1257 (feature_tree), Volumenkörper1258 (feature_tree), Volumenkörper1259 (feature_tree), Volumenkörper1260 (feature_tree), Volumenkörper1261 (feature_tree), Volumenkörper1262 (feature_tree), Volumenkörper1263 (feature_tree), Volumenkörper1264 (feature_tree), Volumenkörper1265 (feature_tree), Volumenkörper1266 (feature_tree), Volumenkörper1267 (feature_tree), Volumenkörper1268 (feature_tree), Volumenkörper1269 (feature_tree), Volumenkörper1270 (feature_tree), Volumenkörper1271 (feature_tree), Volumenkörper1272 (feature_tree), Volumenkörper1273 (feature_tree), Volumenkörper1274 (feature_tree), Volumenkörper1275 (feature_tree), Volumenkörper1276 (feature_tree), Volumenkörper1277 (feature_tree), Volumenkörper1278 (feature_tree), Volumenkörper1279 (feature_tree), Volumenkörper1280 (feature_tree), Volumenkörper1281 (feature_tree), Volumenkörper1282 (feature_tree), Volumenkörper1283 (feature_tree), Volumenkörper1284 (feature_tree), Volumenkörper1285 (feature_tree), Volumenkörper1286 (feature_tree), Volumenkörper1287 (feature_tree), Volumenkörper1288 (feature_tree), Volumenkörper1289 (feature_tree), Volumenkörper1290 (feature_tree), Volumenkörper1291 (feature_tree), Volumenkörper1292 (feature_tree), Volumenkörper1293 (feature_tree), Volumenkörper1294 (feature_tree), Volumenkörper1295 (feature_tree), Volumenkörper1296 (feature_tree), Volumenkörper1297 (feature_tree), Volumenkörper1298 (feature_tree), Volumenkörper1299 (feature_tree), Volumenkörper1300 (feature_tree), Volumenkörper1301 (feature_tree), Volumenkörper1302 (feature_tree), Volumenkörper1303 (feature_tree), Volumenkörper1304 (feature_tree), Volumenkörper1305 (feature_tree), Volumenkörper1306 (feature_tree), Volumenkörper1307 (feature_tree), Volumenkörper1308 (feature_tree), Volumenkörper1309 (feature_tree), Volumenkörper1310 (feature_tree), Volumenkörper1311 (feature_tree), Volumenkörper1312 (feature_tree), Volumenkörper1313 (feature_tree), Volumenkörper1314 (feature_tree), Volumenkörper1315 (feature_tree), Volumenkörper1316 (feature_tree), Volumenkörper1317 (feature_tree), Volumenkörper1318 (feature_tree), Volumenkörper1319 (feature_tree), Volumenkörper1320 (feature_tree), Volumenkörper1321 (feature_tree), Volumenkörper1322 (feature_tree), Volumenkörper1323 (feature_tree), Volumenkörper1324 (feature_tree), Volumenkörper1325 (feature_tree), Volumenkörper1326 (feature_tree), Volumenkörper1327 (feature_tree), Volumenkörper1328 (feature_tree), Volumenkörper1329 (feature_tree), Volumenkörper1330 (feature_tree), Volumenkörper1331 (feature_tree), Volumenkörper1332 (feature_tree), Volumenkörper1333 (feature_tree), Volumenkörper1334 (feature_tree), Volumenkörper1335 (feature_tree), Volumenkörper1336 (feature_tree), Volumenkörper1337 (feature_tree), Volumenkörper1338 (feature_tree), Volumenkörper1339 (feature_tree), Volumenkörper1340 (feature_tree), Volumenkörper1341 (feature_tree), Volumenkörper1342 (feature_tree), Volumenkörper1343 (feature_tree), Volumenkörper1344 (feature_tree), Volumenkörper1345 (feature_tree), Volumenkörper1346 (feature_tree), Volumenkörper1347 (feature_tree), Volumenkörper1348 (feature_tree), Volumenkörper1349 (feature_tree), Volumenkörper1350 (feature_tree), Volumenkörper1351 (feature_tree), Volumenkörper1352 (feature_tree), Volumenkörper1353 (feature_tree), Volumenkörper1354 (feature_tree), Volumenkörper1355 (feature_tree), Volumenkörper1356 (feature_tree), Volumenkörper1357 (feature_tree), Volumenkörper1358 (feature_tree), Volumenkörper1359 (feature_tree), Volumenkörper1360 (feature_tree), Volumenkörper1361 (feature_tree), Volumenkörper1362 (feature_tree), Volumenkörper1363 (feature_tree), Volumenkörper1364 (feature_tree), Volumenkörper1365 (feature_tree), Volumenkörper1366 (feature_tree), Volumenkörper1367 (feature_tree), Volumenkörper1368 (feature_tree), Volumenkörper1369 (feature_tree), Volumenkörper1370 (feature_tree), Volumenkörper1371 (feature_tree), Volumenkörper1372 (feature_tree), Volumenkörper1373 (feature_tree), Volumenkörper1374 (feature_tree), Volumenkörper1375 (feature_tree), Volumenkörper1376 (feature_tree), Volumenkörper1377 (feature_tree), Volumenkörper1378 (feature_tree), Volumenkörper1379 (feature_tree), Volumenkörper1380 (feature_tree), Volumenkörper1381 (feature_tree), Volumenkörper1382 (feature_tree), Volumenkörper1383 (feature_tree), Volumenkörper1384 (feature_tree), Volumenkörper1385 (feature_tree), Volumenkörper1386 (feature_tree), Volumenkörper1387 (feature_tree), Volumenkörper1388 (feature_tree), Volumenkörper1389 (feature_tree), Volumenkörper1390 (feature_tree), Volumenkörper1391 (feature_tree), Volumenkörper1392 (feature_tree), Volumenkörper1393 (feature_tree), Volumenkörper1394 (feature_tree), Volumenkörper1395 (feature_tree), Volumenkörper1396 (feature_tree), Volumenkörper1397 (feature_tree), Volumenkörper1398 (feature_tree), Volumenkörper1399 (feature_tree), Volumenkörper1400 (feature_tree), Volumenkörper1401 (feature_tree), Volumenkörper1402 (feature_tree), Volumenkörper1403 (feature_tree), Volumenkörper1404 (feature_tree), Volumenkörper1405 (feature_tree), Volumenkörper1406 (feature_tree), Volumenkörper1407 (feature_tree), Volumenkörper1408 (feature_tree), Volumenkörper1409 (feature_tree), Volumenkörper1410 (feature_tree), Volumenkörper1411 (feature_tree), Volumenkörper1412 (feature_tree), Volumenkörper1413 (feature_tree), Volumenkörper1414 (feature_tree), Volumenkörper1415 (feature_tree), Volumenkörper1416 (feature_tree), Volumenkörper1417 (feature_tree), Volumenkörper1418 (feature_tree), Volumenkörper1419 (feature_tree), Volumenkörper1420 (feature_tree), Volumenkörper1421 (feature_tree), Volumenkörper1422 (feature_tree), Volumenkörper1423 (feature_tree), Volumenkörper1424 (feature_tree), Volumenkörper1425 (feature_tree), Volumenkörper1426 (feature_tree), Volumenkörper1427 (feature_tree), Volumenkörper1428 (feature_tree), Volumenkörper1429 (feature_tree), Volumenkörper1430 (feature_tree), Volumenkörper1431 (feature_tree), Volumenkörper1432 (feature_tree), Volumenkörper1433 (feature_tree), Volumenkörper1434 (feature_tree), Volumenkörper1435 (feature_tree), Volumenkörper1436 (feature_tree), Volumenkörper1437 (feature_tree), Volumenkörper1438 (feature_tree), Volumenkörper1439 (feature_tree), Volumenkörper1440 (feature_tree), Volumenkörper1441 (feature_tree), Volumenkörper1442 (feature_tree), Volumenkörper1443 (feature_tree), Volumenkörper1444 (feature_tree), Volumenkörper1445 (feature_tree), Volumenkörper1446 (feature_tree), Volumenkörper1447 (feature_tree), Volumenkörper1448 (feature_tree), Volumenkörper1449 (feature_tree), Volumenkörper1450 (feature_tree), Volumenkörper1451 (feature_tree), Volumenkörper1452 (feature_tree), Volumenkörper1453 (feature_tree), Volumenkörper1454 (feature_tree), Volumenkörper1455 (feature_tree), Volumenkörper1456 (feature_tree), Volumenkörper1457 (feature_tree), Volumenkörper1458 (feature_tree), Volumenkörper1459 (feature_tree), Volumenkörper1460 (feature_tree), Volumenkörper1461 (feature_tree), Volumenkörper1462 (feature_tree), Volumenkörper1463 (feature_tree), Volumenkörper1464 (feature_tree), Volumenkörper1465 (feature_tree), Volumenkörper1466 (feature_tree), Volumenkörper1467 (feature_tree), Volumenkörper1468 (feature_tree), Volumenkörper1469 (feature_tree), Volumenkörper1470 (feature_tree), Volumenkörper1471 (feature_tree), Volumenkörper1472 (feature_tree), Volumenkörper1473 (feature_tree), Volumenkörper1474 (feature_tree), Volumenkörper1475 (feature_tree), Volumenkörper1476 (feature_tree), Volumenkörper1477 (feature_tree), Volumenkörper1478 (feature_tree), Volumenkörper1479 (feature_tree), Volumenkörper1480 (feature_tree), Volumenkörper1481 (feature_tree), Volumenkörper1482 (feature_tree), Volumenkörper1483 (feature_tree), Volumenkörper1484 (feature_tree), Volumenkörper1485 (feature_tree), Volumenkörper1486 (feature_tree), Volumenkörper1487 (feature_tree), Volumenkörper1488 (feature_tree), Volumenkörper1489 (feature_tree), Volumenkörper1490 (feature_tree), Volumenkörper1491 (feature_tree), Volumenkörper1492 (feature_tree), Volumenkörper1493 (feature_tree), Volumenkörper1494 (feature_tree), Volumenkörper1495 (feature_tree), Volumenkörper1496 (feature_tree), Volumenkörper1497 (feature_tree), Volumenkörper1498 (feature_tree), Volumenkörper1499 (feature_tree), Volumenkörper1500 (feature_tree), Volumenkörper1501 (feature_tree), Volumenkörper1502 (feature_tree), Volumenkörper1503 (feature_tree), Volumenkörper1504 (feature_tree), Volumenkörper1505 (feature_tree), Volumenkörper1506 (feature_tree), Volumenkörper1507 (feature_tree), Volumenkörper1508 (feature_tree), Volumenkörper1509 (feature_tree), Volumenkörper1510 (feature_tree), Volumenkörper1511 (feature_tree), Volumenkörper1512 (feature_tree), Volumenkörper1513 (feature_tree), Volumenkörper1514 (feature_tree), Volumenkörper1515 (feature_tree), Volumenkörper1516 (feature_tree), Volumenkörper1517 (feature_tree), Volumenkörper1518 (feature_tree), Volumenkörper1519 (feature_tree), Volumenkörper1520 (feature_tree), Volumenkörper1521 (feature_tree), Volumenkörper1522 (feature_tree), Volumenkörper1523 (feature_tree), Volumenkörper1524 (feature_tree), Volumenkörper1525 (feature_tree), Volumenkörper1526 (feature_tree), Volumenkörper1527 (feature_tree), Volumenkörper1528 (feature_tree), Volumenkörper1529 (feature_tree), Volumenkörper1530 (feature_tree), Volumenkörper1531 (feature_tree), Volumenkörper1532 (feature_tree), Volumenkörper1533 (feature_tree), Volumenkörper1534 (feature_tree), Volumenkörper1535 (feature_tree), Volumenkörper1536 (feature_tree), Volumenkörper1537 (feature_tree), Volumenkörper1538 (feature_tree), Volumenkörper1539 (feature_tree), Volumenkörper1540 (feature_tree), Volumenkörper1541 (feature_tree), Volumenkörper1542 (feature_tree), Volumenkörper1543 (feature_tree), Volumenkörper1544 (feature_tree), Volumenkörper1545 (feature_tree), Volumenkörper1546 (feature_tree), Volumenkörper1547 (feature_tree), Volumenkörper1548 (feature_tree), Volumenkörper1549 (feature_tree), Volumenkörper1550 (feature_tree), Volumenkörper1551 (feature_tree), Volumenkörper1552 (feature_tree), Volumenkörper1553 (feature_tree), Volumenkörper1554 (feature_tree), Volumenkörper1555 (feature_tree), Volumenkörper1556 (feature_tree), Volumenkörper1557 (feature_tree), Volumenkörper1558 (feature_tree), Volumenkörper1559 (feature_tree), Volumenkörper1560 (feature_tree), Volumenkörper1561 (feature_tree), Volumenkörper1562 (feature_tree), Volumenkörper1563 (feature_tree), Volumenkörper1564 (feature_tree), Volumenkörper1565 (feature_tree), Volumenkörper1566 (feature_tree), Volumenkörper1567 (feature_tree), Volumenkörper1568 (feature_tree), Volumenkörper1569 (feature_tree), Volumenkörper1570 (feature_tree), Volumenkörper1571 (feature_tree), Volumenkörper1572 (feature_tree), Volumenkörper1573 (feature_tree), Volumenkörper1574 (feature_tree), Volumenkörper1575 (feature_tree), Volumenkörper1576 (feature_tree), Volumenkörper1577 (feature_tree), Volumenkörper1578 (feature_tree), Volumenkörper1579 (feature_tree), Volumenkörper1580 (feature_tree), Volumenkörper1581 (feature_tree), Volumenkörper1582 (feature_tree), Volumenkörper1583 (feature_tree), Volumenkörper1584 (feature_tree), Volumenkörper1585 (feature_tree), Volumenkörper1586 (feature_tree), Volumenkörper1587 (feature_tree), Volumenkörper1588 (feature_tree), Volumenkörper1589 (feature_tree), Volumenkörper1590 (feature_tree), Volumenkörper1591 (feature_tree), Volumenkörper1592 (feature_tree), Volumenkörper1593 (feature_tree), Volumenkörper1594 (feature_tree), Volumenkörper1595 (feature_tree), Volumenkörper1596 (feature_tree), Volumenkörper1597 (feature_tree), Volumenkörper1598 (feature_tree), Volumenkörper1599 (feature_tree), Volumenkörper1600 (feature_tree), Volumenkörper1601 (feature_tree), Volumenkörper1602 (feature_tree), Volumenkörper1603 (feature_tree), Volumenkörper1604 (feature_tree), Volumenkörper1605 (feature_tree), Volumenkörper1606 (feature_tree), Volumenkörper1607 (feature_tree), Volumenkörper1608 (feature_tree), Volumenkörper1609 (feature_tree), Volumenkörper1610 (feature_tree), Volumenkörper1611 (feature_tree), Volumenkörper1612 (feature_tree), Volumenkörper1613 (feature_tree), Volumenkörper1614 (feature_tree), Volumenkörper1615 (feature_tree), Volumenkörper1616 (feature_tree), Volumenkörper1617 (feature_tree), Volumenkörper1618 (feature_tree), Volumenkörper1619 (feature_tree), Volumenkörper1620 (feature_tree), Volumenkörper1621 (feature_tree), Volumenkörper1622 (feature_tree), Volumenkörper1623 (feature_tree), Volumenkörper1624 (feature_tree), Volumenkörper1625 (feature_tree), Volumenkörper1626 (feature_tree), Volumenkörper1627 (feature_tree), Volumenkörper1628 (feature_tree), Volumenkörper1629 (feature_tree), Volumenkörper1630 (feature_tree), Volumenkörper1631 (feature_tree), Volumenkörper1632 (feature_tree), Volumenkörper1633 (feature_tree), Volumenkörper1634 (feature_tree), Volumenkörper1635 (feature_tree), Volumenkörper1636 (feature_tree), Volumenkörper1637 (feature_tree), Volumenkörper1638 (feature_tree), Volumenkörper1639 (feature_tree), Volumenkörper1640 (feature_tree), Volumenkörper1641 (feature_tree), Volumenkörper1642 (feature_tree), Volumenkörper1643 (feature_tree), Volumenkörper1644 (feature_tree), Volumenkörper1645 (feature_tree), Volumenkörper1646 (feature_tree), Volumenkörper1647 (feature_tree), Volumenkörper1648 (feature_tree), Volumenkörper1649 (feature_tree), Volumenkörper1650 (feature_tree), Volumenkörper1651 (feature_tree), Volumenkörper1652 (feature_tree), Volumenkörper1653 (feature_tree), Volumenkörper1654 (feature_tree), Volumenkörper1655 (feature_tree), Volumenkörper1656 (feature_tree), Volumenkörper1657 (feature_tree), Volumenkörper1658 (feature_tree), Volumenkörper1659 (feature_tree), Volumenkörper1660 (feature_tree), Volumenkörper1661 (feature_tree), Volumenkörper1662 (feature_tree), Volumenkörper1663 (feature_tree), Volumenkörper1664 (feature_tree), Volumenkörper1665 (feature_tree), Volumenkörper1666 (feature_tree), Volumenkörper1667 (feature_tree), Volumenkörper1668 (feature_tree), Volumenkörper1669 (feature_tree), Volumenkörper1670 (feature_tree), Volumenkörper1671 (feature_tree), Volumenkörper1672 (feature_tree), Volumenkörper1673 (feature_tree), Volumenkörper1674 (feature_tree), Volumenkörper1675 (feature_tree), Volumenkörper1676 (feature_tree), Volumenkörper1677 (feature_tree), Volumenkörper1678 (feature_tree), Volumenkörper1679 (feature_tree), Volumenkörper1680 (feature_tree), Volumenkörper1681 (feature_tree), Volumenkörper1682 (feature_tree), Volumenkörper1683 (feature_tree), Volumenkörper1684 (feature_tree), Volumenkörper1685 (feature_tree), Volumenkörper1686 (feature_tree), Volumenkörper1687 (feature_tree), Volumenkörper1688 (feature_tree), Volumenkörper1689 (feature_tree), Volumenkörper1690 (feature_tree), Volumenkörper1691 (feature_tree), Volumenkörper1692 (feature_tree), Volumenkörper1693 (feature_tree), Volumenkörper1694 (feature_tree), Volumenkörper1695 (feature_tree), Volumenkörper1696 (feature_tree), Volumenkörper1697 (feature_tree), Volumenkörper1698 (feature_tree), Volumenkörper1699 (feature_tree), Volumenkörper1700 (feature_tree), Volumenkörper1701 (feature_tree), Volumenkörper1702 (feature_tree), Volumenkörper1703 (feature_tree), Volumenkörper1704 (feature_tree), Volumenkörper1705 (feature_tree), Volumenkörper1706 (feature_tree), Volumenkörper1707 (feature_tree), Volumenkörper1708 (feature_tree), Volumenkörper1709 (feature_tree), Volumenkörper1710 (feature_tree), Volumenkörper1711 (feature_tree), Volumenkörper1712 (feature_tree), Volumenkörper1713 (feature_tree), Volumenkörper1714 (feature_tree), Volumenkörper1715 (feature_tree), Volumenkörper1716 (feature_tree), Volumenkörper1717 (feature_tree), Volumenkörper1718 (feature_tree), Volumenkörper1719 (feature_tree), Volumenkörper1720 (feature_tree), Volumenkörper1721 (feature_tree), Volumenkörper1722 (feature_tree), Volumenkörper1723 (feature_tree), Volumenkörper1724 (feature_tree), Volumenkörper1725 (feature_tree), Volumenkörper1726 (feature_tree), Volumenkörper1727 (feature_tree), Volumenkörper1728 (feature_tree), Volumenkörper1729 (feature_tree), Volumenkörper1730 (feature_tree), Volumenkörper1731 (feature_tree), Volumenkörper1732 (feature_tree), Volumenkörper1733 (feature_tree), Volumenkörper1734 (feature_tree), Volumenkörper1735 (feature_tree), Volumenkörper1736 (feature_tree), Volumenkörper1737 (feature_tree), Volumenkörper1738 (feature_tree), Volumenkörper1739 (feature_tree), Volumenkörper1740 (feature_tree), Volumenkörper1741 (feature_tree), Volumenkörper1742 (feature_tree), Volumenkörper1743 (feature_tree), Volumenkörper1744 (feature_tree), Volumenkörper1745 (feature_tree), Volumenkörper1746 (feature_tree), Volumenkörper1747 (feature_tree), Volumenkörper1748 (feature_tree), Volumenkörper1749 (feature_tree), Volumenkörper1750 (feature_tree), Volumenkörper1751 (feature_tree), Volumenkörper1752 (feature_tree), Volumenkörper1753 (feature_tree), Volumenkörper1754 (feature_tree), Volumenkörper1755 (feature_tree), Volumenkörper1756 (feature_tree), Volumenkörper1757 (feature_tree), Volumenkörper1758 (feature_tree), Volumenkörper1759 (feature_tree), Volumenkörper1760 (feature_tree), Volumenkörper1761 (feature_tree), Volumenkörper1762 (feature_tree), Volumenkörper1763 (feature_tree), Volumenkörper1764 (feature_tree), Volumenkörper1765 (feature_tree), Volumenkörper1766 (feature_tree), Volumenkörper1767 (feature_tree), Volumenkörper1768 (feature_tree), Volumenkörper1769 (feature_tree), Volumenkörper1770 (feature_tree), Volumenkörper1771 (feature_tree), Volumenkörper1772 (feature_tree), Volumenkörper1773 (feature_tree), Volumenkörper1774 (feature_tree), Volumenkörper1775 (feature_tree), Volumenkörper1776 (feature_tree), Volumenkörper1777 (feature_tree), Volumenkörper1778 (feature_tree), Volumenkörper1779 (feature_tree), Volumenkörper1780 (feature_tree), Volumenkörper1781 (feature_tree), Volumenkörper1782 (feature_tree), Volumenkörper1783 (feature_tree), Volumenkörper1784 (feature_tree), Volumenkörper1785 (feature_tree), Volumenkörper1786 (feature_tree), Volumenkörper1787 (feature_tree), Volumenkörper1788 (feature_tree), Volumenkörper1789 (feature_tree), Volumenkörper1790 (feature_tree), Volumenkörper1791 (feature_tree), Volumenkörper1792 (feature_tree), Volumenkörper1793 (feature_tree), Volumenkörper1794 (feature_tree), Volumenkörper1795 (feature_tree), Volumenkörper1796 (feature_tree), Volumenkörper1797 (feature_tree), Volumenkörper1798 (feature_tree), Volumenkörper1799 (feature_tree), Volumenkörper1800 (feature_tree), Volumenkörper1801 (feature_tree), Volumenkörper1802 (feature_tree), Volumenkörper1803 (feature_tree), Volumenkörper1804 (feature_tree), Volumenkörper1805 (feature_tree), Volumenkörper1806 (feature_tree), Volumenkörper1807 (feature_tree), Volumenkörper1808 (feature_tree), Volumenkörper1809 (feature_tree), Volumenkörper1810 (feature_tree), Volumenkörper1811 (feature_tree), Volumenkörper1812 (feature_tree), Volumenkörper1813 (feature_tree), Volumenkörper1814 (feature_tree), Volumenkörper1815 (feature_tree), Volumenkörper1816 (feature_tree), Volumenkörper1817 (feature_tree), Volumenkörper1818 (feature_tree), Volumenkörper1819 (feature_tree), Volumenkörper1820 (feature_tree), Volumenkörper1821 (feature_tree), Volumenkörper1822 (feature_tree), Volumenkörper1823 (feature_tree), Volumenkörper1824 (feature_tree), Volumenkörper1825 (feature_tree), Volumenkörper1826 (feature_tree), Volumenkörper1827 (feature_tree), Volumenkörper1828 (feature_tree), Volumenkörper1829 (feature_tree), Volumenkörper1830 (feature_tree), Volumenkörper1831 (feature_tree), Volumenkörper1832 (feature_tree), Volumenkörper1833 (feature_tree), Volumenkörper1834 (feature_tree), Volumenkörper1835 (feature_tree), Volumenkörper1836 (feature_tree), Volumenkörper1837 (feature_tree), Volumenkörper1838 (feature_tree), Volumenkörper1839 (feature_tree), Volumenkörper1840 (feature_tree), Volumenkörper1841 (feature_tree), Volumenkörper1842 (feature_tree), Volumenkörper1843 (feature_tree), Volumenkörper1844 (feature_tree), Volumenkörper1845 (feature_tree), Volumenkörper1846 (feature_tree), Volumenkörper1847 (feature_tree), Volumenkörper1848 (feature_tree), Volumenkörper1849 (feature_tree), Volumenkörper1850 (feature_tree), Volumenkörper1851 (feature_tree), Volumenkörper1852 (feature_tree), Volumenkörper1853 (feature_tree), Volumenkörper1854 (feature_tree), Volumenkörper1855 (feature_tree), Volumenkörper1856 (feature_tree), Volumenkörper1857 (feature_tree), Volumenkörper1858 (feature_tree), Volumenkörper1859 (feature_tree), Volumenkörper1860 (feature_tree), Volumenkörper1861 (feature_tree), Volumenkörper1862 (feature_tree), Volumenkörper1863 (feature_tree), Volumenkörper1864 (feature_tree), Volumenkörper1865 (feature_tree), Volumenkörper1866 (feature_tree), Volumenkörper1867 (feature_tree), Volumenkörper1868 (feature_tree), Volumenkörper1869 (feature_tree), Volumenkörper1870 (feature_tree), Volumenkörper1871 (feature_tree), Volumenkörper1872 (feature_tree), Volumenkörper1873 (feature_tree), Volumenkörper1874 (feature_tree), Volumenkörper1875 (feature_tree), Volumenkörper1876 (feature_tree), Volumenkörper1877 (feature_tree), Volumenkörper1878 (feature_tree), Volumenkörper1879 (feature_tree), Volumenkörper1880 (feature_tree), Volumenkörper1881 (feature_tree), Volumenkörper1882 (feature_tree), Volumenkörper1883 (feature_tree), Volumenkörper1884 (feature_tree), Volumenkörper1885 (feature_tree), Volumenkörper1886 (feature_tree), Volumenkörper1887 (feature_tree), Volumenkörper1888 (feature_tree), Volumenkörper1889 (feature_tree), Volumenkörper1890 (feature_tree), Volumenkörper1891 (feature_tree), Volumenkörper1892 (feature_tree), Volumenkörper1893 (feature_tree), Volumenkörper1894 (feature_tree), Volumenkörper1895 (feature_tree), Volumenkörper1896 (feature_tree), Volumenkörper1897 (feature_tree), Volumenkörper1898 (feature_tree), Volumenkörper1899 (feature_tree), Volumenkörper1900 (feature_tree), Volumenkörper1901 (feature_tree), Volumenkörper1902 (feature_tree), Volumenkörper1903 (feature_tree), Volumenkörper1904 (feature_tree), Volumenkörper1905 (feature_tree), Volumenkörper1906 (feature_tree), Volumenkörper1907 (feature_tree), Volumenkörper1908 (feature_tree), Volumenkörper1909 (feature_tree), Volumenkörper1910 (feature_tree), Volumenkörper1911 (feature_tree), Volumenkörper1912 (feature_tree), Volumenkörper1913 (feature_tree), Volumenkörper1914 (feature_tree), Volumenkörper1915 (feature_tree), Volumenkörper1916 (feature_tree), Volumenkörper1917 (feature_tree), Volumenkörper1918 (feature_tree), Volumenkörper1919 (feature_tree), Volumenkörper1920 (feature_tree), Volumenkörper1921 (feature_tree), Volumenkörper1922 (feature_tree), Volumenkörper1923 (feature_tree), Volumenkörper1924 (feature_tree), Volumenkörper1925 (feature_tree), Volumenkörper1926 (feature_tree), Volumenkörper1927 (feature_tree), Volumenkörper1928 (feature_tree), Volumenkörper1929 (feature_tree), Volumenkörper1930 (feature_tree), Volumenkörper1931 (feature_tree), Volumenkörper1932 (feature_tree), Volumenkörper1933 (feature_tree), Volumenkörper1934 (feature_tree), Volumenkörper1935 (feature_tree), Volumenkörper1936 (feature_tree), Volumenkörper1937 (feature_tree), Volumenkörper1938 (feature_tree), Volumenkörper1939 (feature_tree), Volumenkörper1940 (feature_tree), Volumenkörper1941 (feature_tree), Volumenkörper1942 (feature_tree), Volumenkörper1943 (feature_tree), Volumenkörper1944 (feature_tree), Volumenkörper1945 (feature_tree), Volumenkörper1946 (feature_tree), Volumenkörper1947 (feature_tree), Volumenkörper1948 (feature_tree), Volumenkörper1949 (feature_tree), Volumenkörper1950 (feature_tree), Volumenkörper1951 (feature_tree), Volumenkörper1952 (feature_tree), Volumenkörper1953 (feature_tree), Volumenkörper1954 (feature_tree), Volumenkörper1955 (feature_tree), Volumenkörper1956 (feature_tree), Volumenkörper1957 (feature_tree), Volumenkörper1958 (feature_tree), Volumenkörper1959 (feature_tree), Volumenkörper1960 (feature_tree), Volumenkörper1961 (feature_tree), Volumenkörper1962 (feature_tree), Volumenkörper1963 (feature_tree), Volumenkörper1964 (feature_tree), Volumenkörper1965 (feature_tree), Volumenkörper1966 (feature_tree), Volumenkörper1967 (feature_tree), Volumenkörper1968 (feature_tree), Volumenkörper1969 (feature_tree), Volumenkörper1970 (feature_tree), Volumenkörper1971 (feature_tree), Volumenkörper1972 (feature_tree), Volumenkörper1973 (feature_tree), Volumenkörper1974 (feature_tree), Volumenkörper1975 (feature_tree), Volumenkörper1976 (feature_tree), Volumenkörper1977 (feature_tree), Volumenkörper1978 (feature_tree), Volumenkörper1979 (feature_tree), Volumenkörper1980 (feature_tree), Volumenkörper1981 (feature_tree), Volumenkörper1982 (feature_tree), Volumenkörper1983 (feature_tree), Volumenkörper1984 (feature_tree), Volumenkörper1985 (feature_tree), Volumenkörper1986 (feature_tree), Volumenkörper1987 (feature_tree), Volumenkörper1988 (feature_tree), Volumenkörper1989 (feature_tree), Volumenkörper1990 (feature_tree), Volumenkörper1991 (feature_tree), Volumenkörper1992 (feature_tree), Volumenkörper1993 (feature_tree), Volumenkörper1994 (feature_tree), Volumenkörper1995 (feature_tree), Volumenkörper1996 (feature_tree), Volumenkörper1997 (feature_tree), Volumenkörper1998 (feature_tree), Volumenkörper1999 (feature_tree), Volumenkörper2000 (feature_tree), Volumenkörper2001 (feature_tree), Volumenkörper2002 (feature_tree), Volumenkörper2003 (feature_tree), Volumenkörper2004 (feature_tree), Volumenkörper2005 (feature_tree), Volumenkörper2006 (feature_tree), Volumenkörper2007 (feature_tree), Volumenkörper2008 (feature_tree), Volumenkörper2009 (feature_tree), Volumenkörper2010 (feature_tree), Volumenkörper2011 (feature_tree), Volumenkörper2012 (feature_tree), Volumenkörper2013 (feature_tree), Volumenkörper2014 (feature_tree), Volumenkörper2015 (feature_tree), Volumenkörper2016 (feature_tree), Volumenkörper2017 (feature_tree), Volumenkörper2018 (feature_tree), Volumenkörper2019 (feature_tree), Volumenkörper2020 (feature_tree), Volumenkörper2021 (feature_tree), Volumenkörper2022 (feature_tree), Volumenkörper2023 (feature_tree), Volumenkörper2024 (feature_tree), Volumenkörper2025 (feature_tree), Volumenkörper2026 (feature_tree), Volumenkörper2027 (feature_tree), Volumenkörper2028 (feature_tree), Volumenkörper2029 (feature_tree), Volumenkörper2030 (feature_tree), Volumenkörper2031 (feature_tree), Volumenkörper2032 (feature_tree), Volumenkörper2033 (feature_tree), Volumenkörper2034 (feature_tree), Volumenkörper2035 (feature_tree), Volumenkörper2036 (feature_tree), Volumenkörper2037 (feature_tree), Volumenkörper2038 (feature_tree), Volumenkörper2039 (feature_tree), Volumenkörper2040 (feature_tree), Volumenkörper2041 (feature_tree), Volumenkörper2042 (feature_tree), Volumenkörper2043 (feature_tree), Volumenkörper2044 (feature_tree), Volumenkörper2045 (feature_tree), Volumenkörper2046 (feature_tree), Volumenkörper2047 (feature_tree), Volumenkörper2048 (feature_tree), Volumenkörper2049 (feature_tree), Volumenkörper2050 (feature_tree), Volumenkörper2051 (feature_tree), Volumenkörper2052 (feature_tree), Volumenkörper2053 (feature_tree), Volumenkörper2054 (feature_tree), Volumenkörper2055 (feature_tree), Volumenkörper2056 (feature_tree), Volumenkörper2057 (feature_tree), Volumenkörper2058 (feature_tree), Volumenkörper2059 (feature_tree), Volumenkörper2060 (feature_tree), Volumenkörper2061 (feature_tree), Volumenkörper2062 (feature_tree), Volumenkörper2063 (feature_tree), Volumenkörper2064 (feature_tree), Volumenkörper2065 (feature_tree), Volumenkörper2066 (feature_tree), Volumenkörper2067 (feature_tree), Volumenkörper2068 (feature_tree), Volumenkörper2069 (feature_tree), Volumenkörper2070 (feature_tree), Volumenkörper2071 (feature_tree), Volumenkörper2072 (feature_tree), Volumenkörper2073 (feature_tree), Volumenkörper2074 (feature_tree), Volumenkörper2075 (feature_tree), Volumenkörper2076 (feature_tree), Volumenkörper2077 (feature_tree), Volumenkörper2078 (feature_tree), Volumenkörper2079 (feature_tree), Volumenkörper2080 (feature_tree), Volumenkörper2081 (feature_tree), Volumenkörper2082 (feature_tree), Volumenkörper2083 (feature_tree), Volumenkörper2084 (feature_tree), Volumenkörper2085 (feature_tree), Volumenkörper2086 (feature_tree), Volumenkörper2087 (feature_tree), Volumenkörper2088 (feature_tree), Volumenkörper2089 (feature_tree), Volumenkörper2090 (feature_tree), Volumenkörper2091 (feature_tree), Volumenkörper2092 (feature_tree), Volumenkörper2093 (feature_tree), Volumenkörper2094 (feature_tree), Volumenkörper2095 (feature_tree), Volumenkörper2096 (feature_tree), Volumenkörper2097 (feature_tree), Volumenkörper2098 (feature_tree), Volumenkörper2099 (feature_tree), Volumenkörper2100 (feature_tree), Volumenkörper2101 (feature_tree), Volumenkörper2102 (feature_tree), Volumenkörper2103 (feature_tree), Volumenkörper2104 (feature_tree), Volumenkörper2105 (feature_tree), Volumenkörper2106 (feature_tree), Volumenkörper2107 (feature_tree), Volumenkörper2108 (feature_tree), Volumenkörper2109 (feature_tree), Volumenkörper2110 (feature_tree), Volumenkörper2111 (feature_tree), Volumenkörper2112 (feature_tree), Volumenkörper2113 (feature_tree), Volumenkörper2114 (feature_tree), Volumenkörper2115 (feature_tree), Volumenkörper2116 (feature_tree), Volumenkörper2117 (feature_tree), Volumenkörper2118 (feature_tree), Volumenkörper2119 (feature_tree), Volumenkörper2120 (feature_tree), Volumenkörper2121 (feature_tree), Volumenkörper2122 (feature_tree), Volumenkörper2123 (feature_tree), Volumenkörper2124 (feature_tree), Volumenkörper2125 (feature_tree), Volumenkörper2126 (feature_tree), Volumenkörper2127 (feature_tree), Volumenkörper2128 (feature_tree), Volumenkörper2129 (feature_tree), Volumenkörper2130 (feature_tree), Volumenkörper2131 (feature_tree), Volumenkörper2132 (feature_tree), Volumenkörper2133 (feature_tree), Volumenkörper2134 (feature_tree), Volumenkörper2135 (feature_tree), Volumenkörper2136 (feature_tree), Volumenkörper2137 (feature_tree), Volumenkörper2138 (feature_tree), Volumenkörper2139 (feature_tree), Volumenkörper2140 (feature_tree), Volumenkörper2141 (feature_tree), Volumenkörper2142 (feature_tree), Volumenkörper2143 (feature_tree), Volumenkörper2144 (feature_tree), Volumenkörper2145 (feature_tree), Volumenkörper2146 (feature_tree), Volumenkörper2147 (feature_tree), Volumenkörper2148 (feature_tree), Volumenkörper2149 (feature_tree), Volumenkörper2150 (feature_tree), Volumenkörper2151 (feature_tree), Volumenkörper2152 (feature_tree), Volumenkörper2153 (feature_tree), Volumenkörper2154 (feature_tree), Volumenkörper2155 (feature_tree), Volumenkörper2156 (feature_tree), Volumenkörper2157 (feature_tree), Volumenkörper2158 (feature_tree), Volumenkörper2159 (feature_tree), Volumenkörper2160 (feature_tree), Volumenkörper2161 (feature_tree), Volumenkörper2162 (feature_tree), Volumenkörper2163 (feature_tree), Volumenkörper2164 (feature_tree), Volumenkörper2165 (feature_tree), Volumenkörper2166 (feature_tree), Volumenkörper2167 (feature_tree), Volumenkörper2168 (feature_tree), Volumenkörper2169 (feature_tree), Volumenkörper2170 (feature_tree), Volumenkörper2171 (feature_tree), Volumenkörper2172 (feature_tree), Volumenkörper2173 (feature_tree), Volumenkörper2174 (feature_tree), Volumenkörper2175 (feature_tree), Volumenkörper2176 (feature_tree), Volumenkörper2177 (feature_tree), Volumenkörper2178 (feature_tree), Volumenkörper2179 (feature_tree), Volumenkörper2180 (feature_tree), Volumenkörper2181 (feature_tree), Volumenkörper2182 (feature_tree), Volumenkörper2183 (feature_tree), Volumenkörper2184 (feature_tree), Volumenkörper2185 (feature_tree), Volumenkörper2186 (feature_tree), Volumenkörper2187 (feature_tree), Volumenkörper2188 (feature_tree), Volumenkörper2189 (feature_tree), Volumenkörper2190 (feature_tree), Volumenkörper2191 (feature_tree), Volumenkörper2192 (feature_tree), Volumenkörper2193 (feature_tree), Volumenkörper2194 (feature_tree), Volumenkörper2195 (feature_tree), Volumenkörper2196 (feature_tree), Volumenkörper2197 (feature_tree), Volumenkörper2198 (feature_tree), Volumenkörper2199 (feature_tree), Volumenkörper2200 (feature_tree), Volumenkörper2201 (feature_tree), Volumenkörper2202 (feature_tree), Volumenkörper2203 (feature_tree), Volumenkörper2204 (feature_tree), Volumenkörper2205 (feature_tree), Volumenkörper2206 (feature_tree), Volumenkörper2207 (feature_tree), Volumenkörper2208 (feature_tree), Volumenkörper2209 (feature_tree), Volumenkörper2210 (feature_tree), Volumenkörper2211 (feature_tree), Volumenkörper2212 (feature_tree), Volumenkörper2213 (feature_tree), Volumenkörper2214 (feature_tree), Volumenkörper2215 (feature_tree), Volumenkörper2216 (feature_tree), Volumenkörper2217 (feature_tree), Volumenkörper2218 (feature_tree), Volumenkörper2219 (feature_tree), Volumenkörper2220 (feature_tree), Volumenkörper2221 (feature_tree), Volumenkörper2222 (feature_tree), Volumenkörper2223 (feature_tree), Volumenkörper2224 (feature_tree), Volumenkörper2225 (feature_tree), Volumenkörper2226 (feature_tree), Volumenkörper2227 (feature_tree), Volumenkörper2228 (feature_tree), Volumenkörper2229 (feature_tree), Volumenkörper2230 (feature_tree), Volumenkörper2231 (feature_tree), Volumenkörper2232 (feature_tree), Volumenkörper2233 (feature_tree), Volumenkörper2234 (feature_tree), Volumenkörper2235 (feature_tree), Volumenkörper2236 (feature_tree), Volumenkörper2237 (feature_tree), Volumenkörper2238 (feature_tree), Volumenkörper2239 (feature_tree), Volumenkörper2240 (feature_tree), Volumenkörper2241 (feature_tree), Volumenkörper2242 (feature_tree), Volumenkörper2243 (feature_tree), Volumenkörper2244 (feature_tree), Volumenkörper2245 (feature_tree), Volumenkörper2246 (feature_tree), Volumenkörper2247 (feature_tree), Volumenkörper2248 (feature_tree), Volumenkörper2249 (feature_tree), Volumenkörper2250 (feature_tree), Volumenkörper2251 (feature_tree), Volumenkörper2252 (feature_tree), Volumenkörper2253 (feature_tree), Volumenkörper2254 (feature_tree), Volumenkörper2255 (feature_tree), Volumenkörper2256 (feature_tree), Volumenkörper2257 (feature_tree), Volumenkörper2258 (feature_tree), Volumenkörper2259 (feature_tree), Volumenkörper2260 (feature_tree), Volumenkörper2261 (feature_tree), Volumenkörper2262 (feature_tree), Volumenkörper2263 (feature_tree), Volumenkörper2264 (feature_tree), Volumenkörper2265 (feature_tree), Volumenkörper2266 (feature_tree), Volumenkörper2267 (feature_tree), Volumenkörper2268 (feature_tree), Volumenkörper2269 (feature_tree), Volumenkörper2270 (feature_tree), Volumenkörper2271 (feature_tree), Volumenkörper2272 (feature_tree), Volumenkörper2273 (feature_tree), Volumenkörper2274 (feature_tree), Volumenkörper2275 (feature_tree), Volumenkörper2276 (feature_tree), Volumenkörper2277 (feature_tree), Volumenkörper2278 (feature_tree), Volumenkörper2279 (feature_tree), Volumenkörper2280 (feature_tree), Volumenkörper2281 (feature_tree), Volumenkörper2282 (feature_tree), Volumenkörper2283 (feature_tree), Volumenkörper2284 (feature_tree), Volumenkörper2285 (feature_tree), Volumenkörper2286 (feature_tree), Volumenkörper2287 (feature_tree), Volumenkörper2288 (feature_tree), Volumenkörper2289 (feature_tree), Volumenkörper2290 (feature_tree), Volumenkörper2291 (feature_tree), Volumenkörper2292 (feature_tree), Volumenkörper2293 (feature_tree), Volumenkörper2294 (feature_tree), Volumenkörper2295 (feature_tree), Volumenkörper2296 (feature_tree), Volumenkörper2297 (feature_tree), Volumenkörper2298 (feature_tree), Volumenkörper2299 (feature_tree), Volumenkörper2300 (feature_tree), Volumenkörper2301 (feature_tree), Volumenkörper2302 (feature_tree), Volumenkörper2303 (feature_tree), Volumenkörper2304 (feature_tree), Volumenkörper2305 (feature_tree), Volumenkörper2306 (feature_tree), Volumenkörper2307 (feature_tree), Volumenkörper2308 (feature_tree), Volumenkörper2309 (feature_tree), Volumenkörper2310 (feature_tree), Volumenkörper2311 (feature_tree), Volumenkörper2312 (feature_tree), Volumenkörper2313 (feature_tree), Volumenkörper2314 (feature_tree), Volumenkörper2315 (feature_tree), Volumenkörper2316 (feature_tree), Volumenkörper2317 (feature_tree), Volumenkörper2318 (feature_tree), Volumenkörper2319 (feature_tree), Volumenkörper2320 (feature_tree), Volumenkörper2321 (feature_tree), Volumenkörper2322 (feature_tree), Volumenkörper2323 (feature_tree), Volumenkörper2324 (feature_tree), Volumenkörper2325 (feature_tree), Volumenkörper2326 (feature_tree), Volumenkörper2327 (feature_tree), Volumenkörper2328 (feature_tree), Volumenkörper2329 (feature_tree), Volumenkörper2330 (feature_tree), Volumenkörper2331 (feature_tree), Volumenkörper2332 (feature_tree), Volumenkörper2333 (feature_tree), Volumenkörper2334 (feature_tree), Volumenkörper2335 (feature_tree), Volumenkörper2336 (feature_tree), Volumenkörper2337 (feature_tree), Volumenkörper2338 (feature_tree), Volumenkörper2339 (feature_tree), Volumenkörper2340 (feature_tree), Volumenkörper2341 (feature_tree), Volumenkörper2342 (feature_tree), Volumenkörper2343 (feature_tree), Volumenkörper2344 (feature_tree), Volumenkörper2345 (feature_tree), Volumenkörper2346 (feature_tree), Volumenkörper2347 (feature_tree), Volumenkörper2348 (feature_tree), Volumenkörper2349 (feature_tree), Volumenkörper2350 (feature_tree), Volumenkörper2351 (feature_tree), Volumenkörper2352 (feature_tree), Volumenkörper2353 (feature_tree), Volumenkörper2354 (feature_tree), Volumenkörper2355 (feature_tree), Volumenkörper2356 (feature_tree), Volumenkörper2357 (feature_tree), Volumenkörper2358 (feature_tree), Volumenkörper2359 (feature_tree), Volumenkörper2360 (feature_tree), Volumenkörper2361 (feature_tree), Volumenkörper2362 (feature_tree), Volumenkörper2363 (feature_tree), Volumenkörper2364 (feature_tree), Volumenkörper2365 (feature_tree), Volumenkörper2366 (feature_tree), Volumenkörper2367 (feature_tree), Volumenkörper2368 (feature_tree), Volumenkörper2369 (feature_tree), Volumenkörper2370 (feature_tree), Volumenkörper2371 (feature_tree), Volumenkörper2372 (feature_tree), Volumenkörper2373 (feature_tree), Volumenkörper2374 (feature_tree), Volumenkörper2375 (feature_tree), Volumenkörper2376 (feature_tree), Volumenkörper2377 (feature_tree), Volumenkörper2378 (feature_tree), Volumenkörper2379 (feature_tree), Volumenkörper2380 (feature_tree), Volumenkörper2381 (feature_tree), Volumenkörper2382 (feature_tree), Volumenkörper2383 (feature_tree), Volumenkörper2384 (feature_tree), Volumenkörper2385 (feature_tree), Volumenkörper2386 (feature_tree), Volumenkörper2387 (feature_tree), Volumenkörper2388 (feature_tree), Volumenkörper2389 (feature_tree), Volumenkörper2390 (feature_tree), Volumenkörper2391 (feature_tree), Volumenkörper2392 (feature_tree), Volumenkörper2393 (feature_tree), Volumenkörper2394 (feature_tree), Volumenkörper2395 (feature_tree), Volumenkörper2396 (feature_tree), Volumenkörper2397 (feature_tree), Volumenkörper2398 (feature_tree), Volumenkörper2399 (feature_tree), Volumenkörper2400 (feature_tree), Volumenkörper2401 (feature_tree), Volumenkörper2402 (feature_tree), Volumenkörper2403 (feature_tree), Volumenkörper2404 (feature_tree), Volumenkörper2405 (feature_tree), Volumenkörper2406 (feature_tree), Volumenkörper2407 (feature_tree), Volumenkörper2408 (feature_tree), Volumenkörper2409 (feature_tree), Volumenkörper2410 (feature_tree), Volumenkörper2411 (feature_tree), Volumenkörper2412 (feature_tree), Volumenkörper2413 (feature_tree), Volumenkörper2414 (feature_tree), Volumenkörper2415 (feature_tree), Volumenkörper2416 (feature_tree), Volumenkörper2417 (feature_tree), Volumenkörper2418 (feature_tree), Volumenkörper2419 (feature_tree), Volumenkörper2420 (feature_tree), Volumenkörper2421 (feature_tree), Volumenkörper2422 (feature_tree), Volumenkörper2423 (feature_tree), Volumenkörper2424 (feature_tree), Volumenkörper2425 (feature_tree), Volumenkörper2426 (feature_tree), Volumenkörper2427 (feature_tree), Volumenkörper2428 (feature_tree), Volumenkörper2429 (feature_tree), Volumenkörper2430 (feature_tree), Volumenkörper2431 (feature_tree), Volumenkörper2432 (feature_tree), Volumenkörper2433 (feature_tree), Volumenkörper2434 (feature_tree), Volumenkörper2435 (feature_tree), Volumenkörper2436 (feature_tree), Volumenkörper2437 (feature_tree), Volumenkörper2438 (feature_tree), Volumenkörper2439 (feature_tree), Volumenkörper2440 (feature_tree), Volumenkörper2441 (feature_tree), Volumenkörper2442 (feature_tree), Volumenkörper2443 (feature_tree), Volumenkörper2444 (feature_tree), Volumenkörper2445 (feature_tree), Volumenkörper2446 (feature_tree), Volumenkörper2447 (feature_tree), Volumenkörper2448 (feature_tree), Volumenkörper2449 (feature_tree), Volumenkörper2450 (feature_tree), Volumenkörper2451 (feature_tree), Volumenkörper2452 (feature_tree), Volumenkörper2453 (feature_tree), Volumenkörper2454 (feature_tree), Volumenkörper2455 (feature_tree), Volumenkörper2456 (feature_tree), Volumenkörper2457 (feature_tree), Volumenkörper2458 (feature_tree), Volumenkörper2459 (feature_tree), Volumenkörper2460 (feature_tree), Volumenkörper2461 (feature_tree), Volumenkörper2462 (feature_tree), Volumenkörper2463 (feature_tree), Volumenkörper2464 (feature_tree), Volumenkörper2465 (feature_tree), Volumenkörper2466 (feature_tree), Volumenkörper2467 (feature_tree), Volumenkörper2468 (feature_tree), Volumenkörper2469 (feature_tree), Volumenkörper2470 (feature_tree), Volumenkörper2471 (feature_tree), Volumenkörper2472 (feature_tree), Volumenkörper2473 (feature_tree), Volumenkörper2474 (feature_tree), Volumenkörper2475 (feature_tree), Volumenkörper2476 (feature_tree), Volumenkörper2477 (feature_tree), Volumenkörper2478 (feature_tree), Volumenkörper2479 (feature_tree), Volumenkörper2480 (feature_tree), Volumenkörper2481 (feature_tree), Volumenkörper2482 (feature_tree), Volumenkörper2483 (feature_tree), Volumenkörper2484 (feature_tree), Volumenkörper2485 (feature_tree), Volumenkörper2486 (feature_tree), Volumenkörper2487 (feature_tree), Volumenkörper2488 (feature_tree), Volumenkörper2489 (feature_tree), Volumenkörper2490 (feature_tree), Volumenkörper2491 (feature_tree), Volumenkörper2492 (feature_tree), Volumenkörper2493 (feature_tree), Volumenkörper2494 (feature_tree), Volumenkörper2495 (feature_tree), Volumenkörper2496 (feature_tree), Volumenkörper2497 (feature_tree), Volumenkörper2498 (feature_tree), Volumenkörper2499 (feature_tree), Volumenkörper2500 (feature_tree), Volumenkörper2501 (feature_tree), Volumenkörper2502 (feature_tree), Volumenkörper2503 (feature_tree), Volumenkörper2504 (feature_tree), Volumenkörper2505 (feature_tree), Volumenkörper2506 (feature_tree), Volumenkörper2507 (feature_tree), Volumenkörper2508 (feature_tree), Volumenkörper2509 (feature_tree), Volumenkörper2510 (feature_tree), Volumenkörper2511 (feature_tree), Volumenkörper2512 (feature_tree), Volumenkörper2513 (feature_tree), Volumenkörper2514 (feature_tree), Volumenkörper2515 (feature_tree), Volumenkörper2516 (feature_tree), Volumenkörper2517 (feature_tree), Volumenkörper2518 (feature_tree), Volumenkörper2519 (feature_tree), Volumenkörper2520 (feature_tree), Volumenkörper2521 (feature_tree), Volumenkörper2522 (feature_tree), Volumenkörper2523 (feature_tree), Volumenkörper2524 (feature_tree), Volumenkörper2525 (feature_tree), Volumenkörper2526 (feature_tree), Volumenkörper2527 (feature_tree), Volumenkörper2528 (feature_tree), Volumenkörper2529 (feature_tree), Volumenkörper2530 (feature_tree), Volumenkörper2531 (feature_tree), Volumenkörper2532 (feature_tree), Volumenkörper2533 (feature_tree), Volumenkörper2534 (feature_tree), Volumenkörper2535 (feature_tree), Volumenkörper2536 (feature_tree), Volumenkörper2537 (feature_tree), Volumenkörper2538 (feature_tree), Volumenkörper2539 (feature_tree), Volumenkörper2540 (feature_tree), Volumenkörper2541 (feature_tree), Volumenkörper2542 (feature_tree), Volumenkörper2543 (feature_tree), Volumenkörper2544 (feature_tree), Volumenkörper2545 (feature_tree), Volumenkörper2546 (feature_tree), Volumenkörper2547 (feature_tree), Volumenkörper2548 (feature_tree), Volumenkörper2549 (feature_tree), Volumenkörper2550 (feature_tree), Volumenkörper2551 (feature_tree), Volumenkörper2552 (feature_tree), Volumenkörper2553 (feature_tree), Volumenkörper2554 (feature_tree), Volumenkörper2555 (feature_tree), Volumenkörper2556 (feature_tree), Volumenkörper2557 (feature_tree), Volumenkörper2558 (feature_tree), Volumenkörper2559 (feature_tree), Volumenkörper2560 (feature_tree), Volumenkörper2561 (feature_tree), Volumenkörper2562 (feature_tree), Volumenkörper2563 (feature_tree), Volumenkörper2564 (feature_tree), Volumenkörper2565 (feature_tree), Volumenkörper2566 (feature_tree), Volumenkörper2567 (feature_tree), Volumenkörper2568 (feature_tree), Volumenkörper2569 (feature_tree), Volumenkörper2570 (feature_tree), Volumenkörper2571 (feature_tree), Volumenkörper2572 (feature_tree), Volumenkörper2573 (feature_tree), Volumenkörper2574 (feature_tree), Volumenkörper2575 (feature_tree), Volumenkörper2576 (feature_tree), Volumenkörper2577 (feature_tree), Volumenkörper2578 (feature_tree), Volumenkörper2579 (feature_tree), Volumenkörper2580 (feature_tree), Volumenkörper2581 (feature_tree), Volumenkörper2582 (feature_tree), Volumenkörper2583 (feature_tree), Volumenkörper2584 (feature_tree), Volumenkörper2585 (feature_tree), Volumenkörper2586 (feature_tree), Volumenkörper2587 (feature_tree), Volumenkörper2588 (feature_tree), Volumenkörper2589 (feature_tree), Volumenkörper2590 (feature_tree), Volumenkörper2591 (feature_tree), Volumenkörper2592 (feature_tree), Volumenkörper2593 (feature_tree), Volumenkörper2594 (feature_tree), Volumenkörper2595 (feature_tree), Volumenkörper2596 (feature_tree), Volumenkörper2597 (feature_tree), Volumenkörper2598 (feature_tree), Volumenkörper2599 (feature_tree), Volumenkörper2600 (feature_tree), Volumenkörper2601 (feature_tree), Volumenkörper2602 (feature_tree), Volumenkörper2603 (feature_tree), Volumenkörper2604 (feature_tree), Volumenkörper2605 (feature_tree), Volumenkörper2606 (feature_tree), Volumenkörper2607 (feature_tree), Volumenkörper2608 (feature_tree), Volumenkörper2609 (feature_tree), Volumenkörper2610 (feature_tree), Volumenkörper2611 (feature_tree), Volumenkörper2612 (feature_tree), Volumenkörper2613 (feature_tree), Volumenkörper2614 (feature_tree), Volumenkörper2615 (feature_tree), Volumenkörper2616 (feature_tree), Volumenkörper2617 (feature_tree), Volumenkörper2618 (feature_tree), Volumenkörper2619 (feature_tree), Volumenkörper2620 (feature_tree), Volumenkörper2621 (feature_tree), Volumenkörper2622 (feature_tree), Volumenkörper2623 (feature_tree), Volumenkörper2624 (feature_tree), Volumenkörper2625 (feature_tree), Volumenkörper2626 (feature_tree), Volumenkörper2627 (feature_tree)
feature tree (5):
  other  "Arbeitsachse1"
  other  "Arbeitsachse2"
  extrude  "Extrusion1"  Depth=100.0mm
  pattern_linear  "Rechteckige Anordnung1"  [2 undecoded]
  sketch  "Skizze1"  dims[d0=5.0mm d1=0.0mm d2=100.0mm d4=30.0mm]
note: 2 required parameter values undecoded (feature->parameter linkage not recoverable at this tier; creation-order binding heuristic only, values carry confidence <= 0.55)
